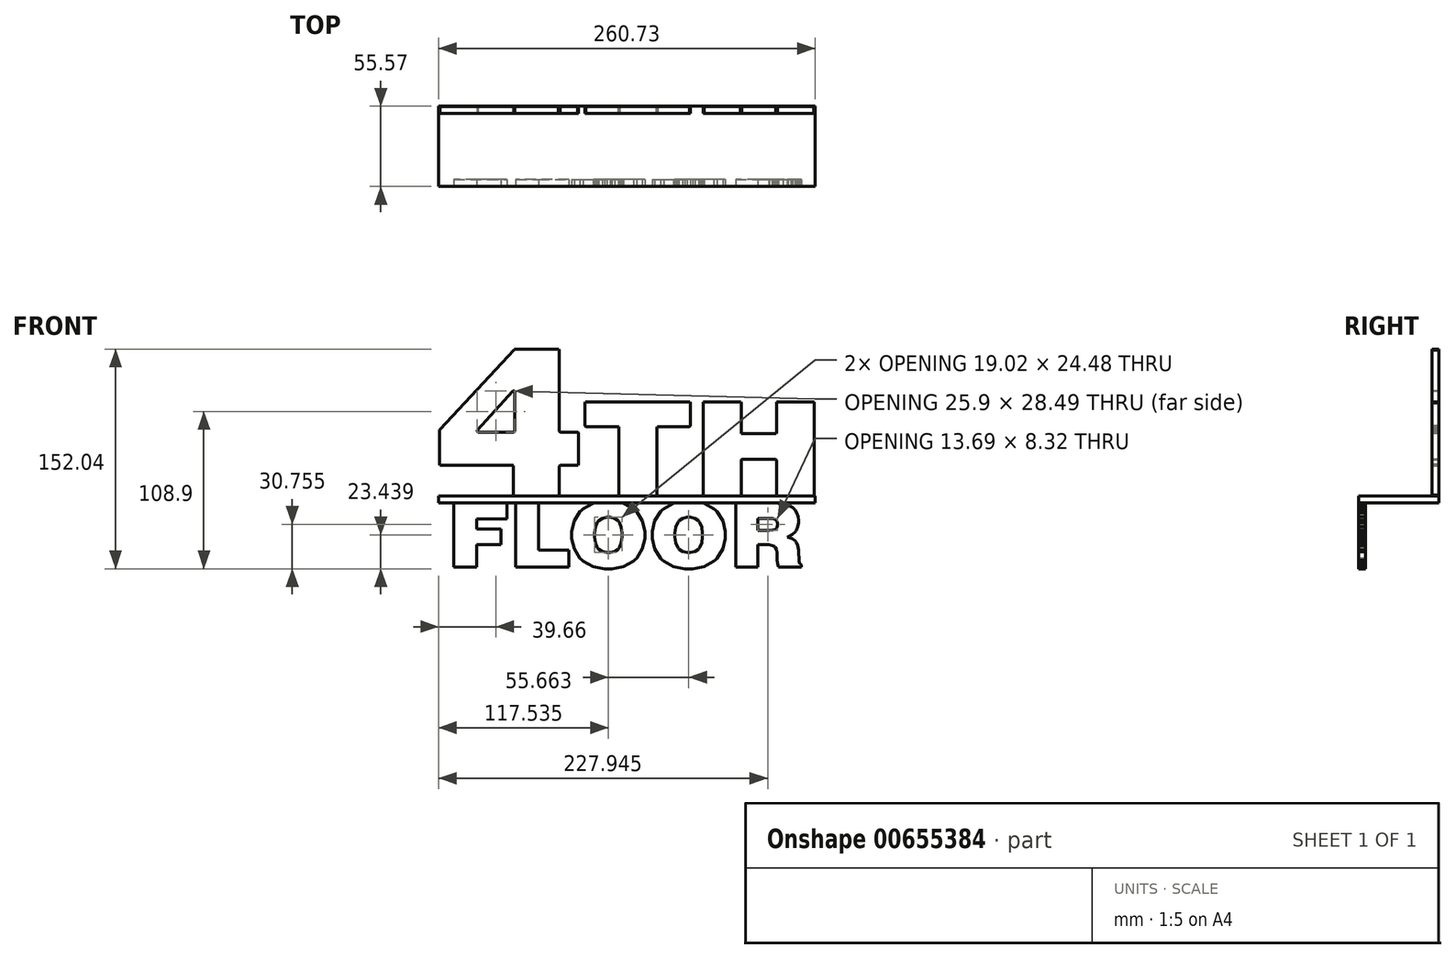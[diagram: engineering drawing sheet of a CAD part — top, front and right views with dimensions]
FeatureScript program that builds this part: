
annotation { "Feature Type Name" : "Feature", "Feature Type Description" : "" }
export const myFeature = defineFeature(function(context is Context, id is Id, definition is map)
    precondition{}
    {
        {
            var Q0;
            Q0=qCreatedBy(makeId("Front.planeOp"),FACE);
            var sketch = newSketch(context, id + "F0", { "sketchPlane" : qUnion([Q0])});
            skLineSegment(sketch, "E0", {"start": v(-106.43, 42.26) * mm, "end": v(-81.93, 42.26) * mm});
            skLineSegment(sketch, "E1", {"start": v(-81.93, 42.26) * mm, "end": v(-81.8, 42.26) * mm});
            skLineSegment(sketch, "E2", {"start": v(-81.8, 42.26) * mm, "end": v(-81.43, 42.48) * mm});
            skLineSegment(sketch, "E3", {"start": v(-81.43, 42.48) * mm, "end": v(-81.22, 42.86) * mm});
            skLineSegment(sketch, "E4", {"start": v(-81.22, 42.86) * mm, "end": v(-81.22, 42.98) * mm});
            skLineSegment(sketch, "E5", {"start": v(-81.22, 42.98) * mm, "end": v(-81.22, 70.06) * mm});
            skLineSegment(sketch, "E6", {"start": v(-81.22, 70.06) * mm, "end": v(-81.22, 70.23) * mm});
            skLineSegment(sketch, "E7", {"start": v(-81.22, 70.23) * mm, "end": v(-81.6, 70.7) * mm});
            skLineSegment(sketch, "E8", {"start": v(-81.6, 70.7) * mm, "end": v(-81.68, 70.73) * mm});
            skLineSegment(sketch, "E9", {"start": v(-81.68, 70.73) * mm, "end": v(-81.75, 70.76) * mm});
            skLineSegment(sketch, "E10", {"start": v(-81.75, 70.76) * mm, "end": v(-82.41, 70.6) * mm});
            skLineSegment(sketch, "E11", {"start": v(-82.41, 70.6) * mm, "end": v(-82.46, 70.54) * mm});
            skLineSegment(sketch, "E12", {"start": v(-82.46, 70.54) * mm, "end": v(-106.97, 43.46) * mm});
            skLineSegment(sketch, "E13", {"start": v(-106.97, 43.46) * mm, "end": v(-107.01, 43.4) * mm});
            skLineSegment(sketch, "E14", {"start": v(-107.01, 43.4) * mm, "end": v(-107.12, 42.75) * mm});
            skLineSegment(sketch, "E15", {"start": v(-107.12, 42.75) * mm, "end": v(-107.1, 42.69) * mm});
            skLineSegment(sketch, "E16", {"start": v(-107.1, 42.69) * mm, "end": v(-107.06, 42.62) * mm});
            skLineSegment(sketch, "E17", {"start": v(-107.06, 42.62) * mm, "end": v(-106.6, 42.26) * mm});
            skLineSegment(sketch, "E18", {"start": v(-106.6, 42.26) * mm, "end": v(-106.43, 42.26) * mm});
            skLineSegment(sketch, "E19", {"start": v(-81.98, -1.24) * mm, "end": v(-81.98, 18.49) * mm});
            skLineSegment(sketch, "E20", {"start": v(-81.98, 18.49) * mm, "end": v(-81.98, 18.61) * mm});
            skLineSegment(sketch, "E21", {"start": v(-81.98, 18.61) * mm, "end": v(-82.2, 19) * mm});
            skLineSegment(sketch, "E22", {"start": v(-82.2, 19) * mm, "end": v(-82.58, 19.2) * mm});
            skLineSegment(sketch, "E23", {"start": v(-82.58, 19.2) * mm, "end": v(-82.7, 19.2) * mm});
            skLineSegment(sketch, "E24", {"start": v(-82.7, 19.2) * mm, "end": v(-132.44, 19.2) * mm});
            skLineSegment(sketch, "E25", {"start": v(-132.44, 19.2) * mm, "end": v(-132.57, 19.2) * mm});
            skLineSegment(sketch, "E26", {"start": v(-132.57, 19.2) * mm, "end": v(-132.95, 19.4) * mm});
            skLineSegment(sketch, "E27", {"start": v(-132.95, 19.4) * mm, "end": v(-133.16, 19.8) * mm});
            skLineSegment(sketch, "E28", {"start": v(-133.16, 19.8) * mm, "end": v(-133.16, 19.92) * mm});
            skLineSegment(sketch, "E29", {"start": v(-133.16, 19.92) * mm, "end": v(-133.16, 43.55) * mm});
            skLineSegment(sketch, "E30", {"start": v(-133.16, 43.55) * mm, "end": v(-133.16, 43.67) * mm});
            skLineSegment(sketch, "E31", {"start": v(-133.16, 43.67) * mm, "end": v(-133, 44) * mm});
            skLineSegment(sketch, "E32", {"start": v(-133, 44) * mm, "end": v(-132.97, 44.04) * mm});
            skLineSegment(sketch, "E33", {"start": v(-132.97, 44.04) * mm, "end": v(-81.43, 99.42) * mm});
            skLineSegment(sketch, "E34", {"start": v(-81.43, 99.42) * mm, "end": v(-81.4, 99.46) * mm});
            skLineSegment(sketch, "E35", {"start": v(-81.4, 99.46) * mm, "end": v(-81.03, 99.65) * mm});
            skLineSegment(sketch, "E36", {"start": v(-81.03, 99.65) * mm, "end": v(-80.9, 99.65) * mm});
            skLineSegment(sketch, "E37", {"start": v(-80.9, 99.65) * mm, "end": v(-51, 99.65) * mm});
            skLineSegment(sketch, "E38", {"start": v(-51, 99.65) * mm, "end": v(-50.88, 99.65) * mm});
            skLineSegment(sketch, "E39", {"start": v(-50.88, 99.65) * mm, "end": v(-50.5, 99.44) * mm});
            skLineSegment(sketch, "E40", {"start": v(-50.5, 99.44) * mm, "end": v(-50.29, 99.06) * mm});
            skLineSegment(sketch, "E41", {"start": v(-50.29, 99.06) * mm, "end": v(-50.29, 98.93) * mm});
            skLineSegment(sketch, "E42", {"start": v(-50.29, 98.93) * mm, "end": v(-50.29, 42.98) * mm});
            skLineSegment(sketch, "E43", {"start": v(-50.29, 42.98) * mm, "end": v(-50.29, 42.86) * mm});
            skLineSegment(sketch, "E44", {"start": v(-50.29, 42.86) * mm, "end": v(-50.08, 42.48) * mm});
            skLineSegment(sketch, "E45", {"start": v(-50.08, 42.48) * mm, "end": v(-49.7, 42.26) * mm});
            skLineSegment(sketch, "E46", {"start": v(-49.7, 42.26) * mm, "end": v(-49.57, 42.26) * mm});
            skLineSegment(sketch, "E47", {"start": v(-49.57, 42.26) * mm, "end": v(-37.82, 42.26) * mm});
            skLineSegment(sketch, "E48", {"start": v(-37.82, 42.26) * mm, "end": v(-37.7, 42.26) * mm});
            skLineSegment(sketch, "E49", {"start": v(-37.7, 42.26) * mm, "end": v(-37.32, 42.05) * mm});
            skLineSegment(sketch, "E50", {"start": v(-37.32, 42.05) * mm, "end": v(-37.1, 41.67) * mm});
            skLineSegment(sketch, "E51", {"start": v(-37.1, 41.67) * mm, "end": v(-37.1, 41.54) * mm});
            skLineSegment(sketch, "E52", {"start": v(-37.1, 41.54) * mm, "end": v(-37.1, 19.92) * mm});
            skLineSegment(sketch, "E53", {"start": v(-37.1, 19.92) * mm, "end": v(-37.1, 19.8) * mm});
            skLineSegment(sketch, "E54", {"start": v(-37.1, 19.8) * mm, "end": v(-37.32, 19.4) * mm});
            skLineSegment(sketch, "E55", {"start": v(-37.32, 19.4) * mm, "end": v(-37.7, 19.2) * mm});
            skLineSegment(sketch, "E56", {"start": v(-37.7, 19.2) * mm, "end": v(-37.82, 19.2) * mm});
            skLineSegment(sketch, "E57", {"start": v(-37.82, 19.2) * mm, "end": v(-49.57, 19.2) * mm});
            skLineSegment(sketch, "E58", {"start": v(-49.57, 19.2) * mm, "end": v(-49.7, 19.2) * mm});
            skLineSegment(sketch, "E59", {"start": v(-49.7, 19.2) * mm, "end": v(-50.08, 19) * mm});
            skLineSegment(sketch, "E60", {"start": v(-50.08, 19) * mm, "end": v(-50.29, 18.61) * mm});
            skLineSegment(sketch, "E61", {"start": v(-50.29, 18.61) * mm, "end": v(-50.29, 18.49) * mm});
            skLineSegment(sketch, "E62", {"start": v(-50.29, 18.49) * mm, "end": v(-50.29, -1.24) * mm});
            skLineSegment(sketch, "E63", {"start": v(-50.29, -1.24) * mm, "end": v(-50.29, -1.36) * mm});
            skLineSegment(sketch, "E64", {"start": v(-50.29, -1.36) * mm, "end": v(-50.5, -1.74) * mm});
            skLineSegment(sketch, "E65", {"start": v(-50.5, -1.74) * mm, "end": v(-50.88, -1.95) * mm});
            skLineSegment(sketch, "E66", {"start": v(-50.88, -1.95) * mm, "end": v(-51, -1.95) * mm});
            skLineSegment(sketch, "E67", {"start": v(-51, -1.95) * mm, "end": v(-81.27, -1.95) * mm});
            skLineSegment(sketch, "E68", {"start": v(-81.27, -1.95) * mm, "end": v(-81.4, -1.95) * mm});
            skLineSegment(sketch, "E69", {"start": v(-81.4, -1.95) * mm, "end": v(-81.77, -1.74) * mm});
            skLineSegment(sketch, "E70", {"start": v(-81.77, -1.74) * mm, "end": v(-81.98, -1.36) * mm});
            skLineSegment(sketch, "E71", {"start": v(-81.98, -1.36) * mm, "end": v(-81.98, -1.24) * mm});
            skLineSegment(sketch, "E72", {"start": v(-8.96, -1.24) * mm, "end": v(-8.96, 45.3) * mm});
            skLineSegment(sketch, "E73", {"start": v(-8.96, 45.3) * mm, "end": v(-8.96, 45.43) * mm});
            skLineSegment(sketch, "E74", {"start": v(-8.96, 45.43) * mm, "end": v(-9.17, 45.81) * mm});
            skLineSegment(sketch, "E75", {"start": v(-9.17, 45.81) * mm, "end": v(-9.55, 46.02) * mm});
            skLineSegment(sketch, "E76", {"start": v(-9.55, 46.02) * mm, "end": v(-9.68, 46.02) * mm});
            skLineSegment(sketch, "E77", {"start": v(-9.68, 46.02) * mm, "end": v(-31.78, 46.02) * mm});
            skLineSegment(sketch, "E78", {"start": v(-31.78, 46.02) * mm, "end": v(-31.91, 46.02) * mm});
            skLineSegment(sketch, "E79", {"start": v(-31.91, 46.02) * mm, "end": v(-32.3, 46.23) * mm});
            skLineSegment(sketch, "E80", {"start": v(-32.3, 46.23) * mm, "end": v(-32.5, 46.61) * mm});
            skLineSegment(sketch, "E81", {"start": v(-32.5, 46.61) * mm, "end": v(-32.5, 46.74) * mm});
            skLineSegment(sketch, "E82", {"start": v(-32.5, 46.74) * mm, "end": v(-32.5, 62.47) * mm});
            skLineSegment(sketch, "E83", {"start": v(-32.5, 62.47) * mm, "end": v(-32.5, 62.6) * mm});
            skLineSegment(sketch, "E84", {"start": v(-32.5, 62.6) * mm, "end": v(-32.3, 62.97) * mm});
            skLineSegment(sketch, "E85", {"start": v(-32.3, 62.97) * mm, "end": v(-31.91, 63.18) * mm});
            skLineSegment(sketch, "E86", {"start": v(-31.91, 63.18) * mm, "end": v(-31.78, 63.18) * mm});
            skLineSegment(sketch, "E87", {"start": v(-31.78, 63.18) * mm, "end": v(39.64, 63.18) * mm});
            skLineSegment(sketch, "E88", {"start": v(39.64, 63.18) * mm, "end": v(39.77, 63.18) * mm});
            skLineSegment(sketch, "E89", {"start": v(39.77, 63.18) * mm, "end": v(40.15, 62.97) * mm});
            skLineSegment(sketch, "E90", {"start": v(40.15, 62.97) * mm, "end": v(40.36, 62.6) * mm});
            skLineSegment(sketch, "E91", {"start": v(40.36, 62.6) * mm, "end": v(40.36, 62.47) * mm});
            skLineSegment(sketch, "E92", {"start": v(40.36, 62.47) * mm, "end": v(40.36, 46.74) * mm});
            skLineSegment(sketch, "E93", {"start": v(40.36, 46.74) * mm, "end": v(40.36, 46.61) * mm});
            skLineSegment(sketch, "E94", {"start": v(40.36, 46.61) * mm, "end": v(40.15, 46.23) * mm});
            skLineSegment(sketch, "E95", {"start": v(40.15, 46.23) * mm, "end": v(39.77, 46.02) * mm});
            skLineSegment(sketch, "E96", {"start": v(39.77, 46.02) * mm, "end": v(39.64, 46.02) * mm});
            skLineSegment(sketch, "E97", {"start": v(39.64, 46.02) * mm, "end": v(18.03, 46.02) * mm});
            skLineSegment(sketch, "E98", {"start": v(18.03, 46.02) * mm, "end": v(17.9, 46.02) * mm});
            skLineSegment(sketch, "E99", {"start": v(17.9, 46.02) * mm, "end": v(17.52, 45.81) * mm});
            skLineSegment(sketch, "E100", {"start": v(17.52, 45.81) * mm, "end": v(17.31, 45.43) * mm});
            skLineSegment(sketch, "E101", {"start": v(17.31, 45.43) * mm, "end": v(17.31, 45.3) * mm});
            skLineSegment(sketch, "E102", {"start": v(17.31, 45.3) * mm, "end": v(17.31, -1.24) * mm});
            skLineSegment(sketch, "E103", {"start": v(17.31, -1.24) * mm, "end": v(17.31, -1.36) * mm});
            skLineSegment(sketch, "E104", {"start": v(17.31, -1.36) * mm, "end": v(17.1, -1.75) * mm});
            skLineSegment(sketch, "E105", {"start": v(17.1, -1.75) * mm, "end": v(16.72, -1.96) * mm});
            skLineSegment(sketch, "E106", {"start": v(16.72, -1.96) * mm, "end": v(16.6, -1.96) * mm});
            skLineSegment(sketch, "E107", {"start": v(16.6, -1.96) * mm, "end": v(-8.24, -1.96) * mm});
            skLineSegment(sketch, "E108", {"start": v(-8.24, -1.96) * mm, "end": v(-8.37, -1.96) * mm});
            skLineSegment(sketch, "E109", {"start": v(-8.37, -1.96) * mm, "end": v(-8.75, -1.75) * mm});
            skLineSegment(sketch, "E110", {"start": v(-8.75, -1.75) * mm, "end": v(-8.96, -1.36) * mm});
            skLineSegment(sketch, "E111", {"start": v(-8.96, -1.36) * mm, "end": v(-8.96, -1.24) * mm});
            skLineSegment(sketch, "E112", {"start": v(49.34, -1.24) * mm, "end": v(49.34, 62.47) * mm});
            skLineSegment(sketch, "E113", {"start": v(49.34, 62.47) * mm, "end": v(49.34, 62.6) * mm});
            skLineSegment(sketch, "E114", {"start": v(49.34, 62.6) * mm, "end": v(49.55, 62.97) * mm});
            skLineSegment(sketch, "E115", {"start": v(49.55, 62.97) * mm, "end": v(49.93, 63.18) * mm});
            skLineSegment(sketch, "E116", {"start": v(49.93, 63.18) * mm, "end": v(50.06, 63.18) * mm});
            skLineSegment(sketch, "E117", {"start": v(50.06, 63.18) * mm, "end": v(74.9, 63.18) * mm});
            skLineSegment(sketch, "E118", {"start": v(74.9, 63.18) * mm, "end": v(75.02, 63.18) * mm});
            skLineSegment(sketch, "E119", {"start": v(75.02, 63.18) * mm, "end": v(75.4, 62.97) * mm});
            skLineSegment(sketch, "E120", {"start": v(75.4, 62.97) * mm, "end": v(75.61, 62.6) * mm});
            skLineSegment(sketch, "E121", {"start": v(75.61, 62.6) * mm, "end": v(75.61, 62.47) * mm});
            skLineSegment(sketch, "E122", {"start": v(75.61, 62.47) * mm, "end": v(75.61, 41.78) * mm});
            skLineSegment(sketch, "E123", {"start": v(75.61, 41.78) * mm, "end": v(75.61, 41.66) * mm});
            skLineSegment(sketch, "E124", {"start": v(75.61, 41.66) * mm, "end": v(75.82, 41.28) * mm});
            skLineSegment(sketch, "E125", {"start": v(75.82, 41.28) * mm, "end": v(76.2, 41.07) * mm});
            skLineSegment(sketch, "E126", {"start": v(76.2, 41.07) * mm, "end": v(76.33, 41.07) * mm});
            skLineSegment(sketch, "E127", {"start": v(76.33, 41.07) * mm, "end": v(99.37, 41.07) * mm});
            skLineSegment(sketch, "E128", {"start": v(99.37, 41.07) * mm, "end": v(99.5, 41.07) * mm});
            skLineSegment(sketch, "E129", {"start": v(99.5, 41.07) * mm, "end": v(99.88, 41.28) * mm});
            skLineSegment(sketch, "E130", {"start": v(99.88, 41.28) * mm, "end": v(100.09, 41.66) * mm});
            skLineSegment(sketch, "E131", {"start": v(100.09, 41.66) * mm, "end": v(100.09, 41.78) * mm});
            skLineSegment(sketch, "E132", {"start": v(100.09, 41.78) * mm, "end": v(100.09, 62.47) * mm});
            skLineSegment(sketch, "E133", {"start": v(100.09, 62.47) * mm, "end": v(100.09, 62.6) * mm});
            skLineSegment(sketch, "E134", {"start": v(100.09, 62.6) * mm, "end": v(100.3, 62.97) * mm});
            skLineSegment(sketch, "E135", {"start": v(100.3, 62.97) * mm, "end": v(100.67, 63.18) * mm});
            skLineSegment(sketch, "E136", {"start": v(100.67, 63.18) * mm, "end": v(100.8, 63.18) * mm});
            skLineSegment(sketch, "E137", {"start": v(100.8, 63.18) * mm, "end": v(125.64, 63.18) * mm});
            skLineSegment(sketch, "E138", {"start": v(125.64, 63.18) * mm, "end": v(125.77, 63.18) * mm});
            skLineSegment(sketch, "E139", {"start": v(125.77, 63.18) * mm, "end": v(126.15, 62.97) * mm});
            skLineSegment(sketch, "E140", {"start": v(126.15, 62.97) * mm, "end": v(126.36, 62.6) * mm});
            skLineSegment(sketch, "E141", {"start": v(126.36, 62.6) * mm, "end": v(126.36, 62.47) * mm});
            skLineSegment(sketch, "E142", {"start": v(126.36, 62.47) * mm, "end": v(126.36, -1.24) * mm});
            skLineSegment(sketch, "E143", {"start": v(126.36, -1.24) * mm, "end": v(126.36, -1.36) * mm});
            skLineSegment(sketch, "E144", {"start": v(126.36, -1.36) * mm, "end": v(126.15, -1.75) * mm});
            skLineSegment(sketch, "E145", {"start": v(126.15, -1.75) * mm, "end": v(125.77, -1.96) * mm});
            skLineSegment(sketch, "E146", {"start": v(125.77, -1.96) * mm, "end": v(125.64, -1.96) * mm});
            skLineSegment(sketch, "E147", {"start": v(125.64, -1.96) * mm, "end": v(100.8, -1.96) * mm});
            skLineSegment(sketch, "E148", {"start": v(100.8, -1.96) * mm, "end": v(100.67, -1.96) * mm});
            skLineSegment(sketch, "E149", {"start": v(100.67, -1.96) * mm, "end": v(100.3, -1.75) * mm});
            skLineSegment(sketch, "E150", {"start": v(100.3, -1.75) * mm, "end": v(100.09, -1.36) * mm});
            skLineSegment(sketch, "E151", {"start": v(100.09, -1.36) * mm, "end": v(100.09, -1.24) * mm});
            skLineSegment(sketch, "E152", {"start": v(100.09, -1.24) * mm, "end": v(100.09, 22.57) * mm});
            skLineSegment(sketch, "E153", {"start": v(100.09, 22.57) * mm, "end": v(100.09, 22.7) * mm});
            skLineSegment(sketch, "E154", {"start": v(100.09, 22.7) * mm, "end": v(99.88, 23.07) * mm});
            skLineSegment(sketch, "E155", {"start": v(99.88, 23.07) * mm, "end": v(99.5, 23.28) * mm});
            skLineSegment(sketch, "E156", {"start": v(99.5, 23.28) * mm, "end": v(99.37, 23.28) * mm});
            skLineSegment(sketch, "E157", {"start": v(99.37, 23.28) * mm, "end": v(76.33, 23.28) * mm});
            skLineSegment(sketch, "E158", {"start": v(76.33, 23.28) * mm, "end": v(76.2, 23.28) * mm});
            skLineSegment(sketch, "E159", {"start": v(76.2, 23.28) * mm, "end": v(75.82, 23.07) * mm});
            skLineSegment(sketch, "E160", {"start": v(75.82, 23.07) * mm, "end": v(75.61, 22.7) * mm});
            skLineSegment(sketch, "E161", {"start": v(75.61, 22.7) * mm, "end": v(75.61, 22.57) * mm});
            skLineSegment(sketch, "E162", {"start": v(75.61, 22.57) * mm, "end": v(75.61, -1.24) * mm});
            skLineSegment(sketch, "E163", {"start": v(75.61, -1.24) * mm, "end": v(75.61, -1.36) * mm});
            skLineSegment(sketch, "E164", {"start": v(75.61, -1.36) * mm, "end": v(75.4, -1.75) * mm});
            skLineSegment(sketch, "E165", {"start": v(75.4, -1.75) * mm, "end": v(75.02, -1.96) * mm});
            skLineSegment(sketch, "E166", {"start": v(75.02, -1.96) * mm, "end": v(74.9, -1.96) * mm});
            skLineSegment(sketch, "E167", {"start": v(74.9, -1.96) * mm, "end": v(50.06, -1.96) * mm});
            skLineSegment(sketch, "E168", {"start": v(50.06, -1.96) * mm, "end": v(49.93, -1.96) * mm});
            skLineSegment(sketch, "E169", {"start": v(49.93, -1.96) * mm, "end": v(49.55, -1.75) * mm});
            skLineSegment(sketch, "E170", {"start": v(49.55, -1.75) * mm, "end": v(49.34, -1.36) * mm});
            skLineSegment(sketch, "E171", {"start": v(49.34, -1.36) * mm, "end": v(49.34, -1.24) * mm});
            skLineSegment(sketch, "E172", {"start": v(-27.6, -75.9) * mm, "end": v(-27.6, -44.7) * mm});
            skLineSegment(sketch, "E173", {"start": v(-27.6, -44.7) * mm, "end": v(-1.73, -44.7) * mm});
            skLineSegment(sketch, "E174", {"start": v(-1.73, -44.7) * mm, "end": v(-1.73, -52.55) * mm});
            skLineSegment(sketch, "E175", {"start": v(-1.73, -52.55) * mm, "end": v(-16.61, -52.55) * mm});
            skLineSegment(sketch, "E176", {"start": v(-16.61, -52.55) * mm, "end": v(-16.61, -57.38) * mm});
            skLineSegment(sketch, "E177", {"start": v(-16.61, -57.38) * mm, "end": v(-4.78, -57.38) * mm});
            skLineSegment(sketch, "E178", {"start": v(-4.78, -57.38) * mm, "end": v(-4.78, -64.93) * mm});
            skLineSegment(sketch, "E179", {"start": v(-4.78, -64.93) * mm, "end": v(-16.61, -64.93) * mm});
            skLineSegment(sketch, "E180", {"start": v(-16.61, -64.93) * mm, "end": v(-16.61, -75.9) * mm});
            skLineSegment(sketch, "E181", {"start": v(-16.61, -75.9) * mm, "end": v(-27.6, -75.9) * mm});
            skLineSegment(sketch, "E182", {"start": v(2.45, -75.9) * mm, "end": v(2.45, -44.7) * mm});
            skLineSegment(sketch, "E183", {"start": v(2.45, -44.7) * mm, "end": v(13.43, -44.7) * mm});
            skLineSegment(sketch, "E184", {"start": v(13.43, -44.7) * mm, "end": v(13.43, -67.61) * mm});
            skLineSegment(sketch, "E185", {"start": v(13.43, -67.61) * mm, "end": v(28.36, -67.61) * mm});
            skLineSegment(sketch, "E186", {"start": v(28.36, -67.61) * mm, "end": v(28.36, -75.9) * mm});
            skLineSegment(sketch, "E187", {"start": v(28.36, -75.9) * mm, "end": v(2.45, -75.9) * mm});
            skLineSegment(sketch, "E188", {"start": v(40.75, -60.32) * mm, "end": v(40.75, -61.28) * mm});
            skLineSegment(sketch, "E189", {"start": v(40.75, -61.28) * mm, "end": v(41.15, -64.16) * mm});
            skLineSegment(sketch, "E190", {"start": v(41.15, -64.16) * mm, "end": v(42.1, -66.48) * mm});
            skLineSegment(sketch, "E191", {"start": v(42.1, -66.48) * mm, "end": v(42.38, -66.83) * mm});
            skLineSegment(sketch, "E192", {"start": v(42.38, -66.83) * mm, "end": v(42.65, -67.18) * mm});
            skLineSegment(sketch, "E193", {"start": v(42.65, -67.18) * mm, "end": v(44.46, -68.38) * mm});
            skLineSegment(sketch, "E194", {"start": v(44.46, -68.38) * mm, "end": v(46.71, -68.9) * mm});
            skLineSegment(sketch, "E195", {"start": v(46.71, -68.9) * mm, "end": v(47.46, -68.9) * mm});
            skLineSegment(sketch, "E196", {"start": v(47.46, -68.9) * mm, "end": v(48.2, -68.9) * mm});
            skLineSegment(sketch, "E197", {"start": v(48.2, -68.9) * mm, "end": v(50.44, -68.39) * mm});
            skLineSegment(sketch, "E198", {"start": v(50.44, -68.39) * mm, "end": v(52.23, -67.18) * mm});
            skLineSegment(sketch, "E199", {"start": v(52.23, -67.18) * mm, "end": v(52.5, -66.84) * mm});
            skLineSegment(sketch, "E200", {"start": v(52.5, -66.84) * mm, "end": v(52.77, -66.5) * mm});
            skLineSegment(sketch, "E201", {"start": v(52.77, -66.5) * mm, "end": v(53.7, -64.18) * mm});
            skLineSegment(sketch, "E202", {"start": v(53.7, -64.18) * mm, "end": v(54.1, -61.28) * mm});
            skLineSegment(sketch, "E203", {"start": v(54.1, -61.28) * mm, "end": v(54.1, -60.32) * mm});
            skLineSegment(sketch, "E204", {"start": v(54.1, -60.32) * mm, "end": v(54.1, -59.35) * mm});
            skLineSegment(sketch, "E205", {"start": v(54.1, -59.35) * mm, "end": v(53.7, -56.45) * mm});
            skLineSegment(sketch, "E206", {"start": v(53.7, -56.45) * mm, "end": v(52.77, -54.13) * mm});
            skLineSegment(sketch, "E207", {"start": v(52.77, -54.13) * mm, "end": v(52.5, -53.79) * mm});
            skLineSegment(sketch, "E208", {"start": v(52.5, -53.79) * mm, "end": v(52.23, -53.44) * mm});
            skLineSegment(sketch, "E209", {"start": v(52.23, -53.44) * mm, "end": v(50.44, -52.23) * mm});
            skLineSegment(sketch, "E210", {"start": v(50.44, -52.23) * mm, "end": v(48.2, -51.72) * mm});
            skLineSegment(sketch, "E211", {"start": v(48.2, -51.72) * mm, "end": v(47.46, -51.72) * mm});
            skLineSegment(sketch, "E212", {"start": v(47.46, -51.72) * mm, "end": v(46.71, -51.72) * mm});
            skLineSegment(sketch, "E213", {"start": v(46.71, -51.72) * mm, "end": v(44.46, -52.24) * mm});
            skLineSegment(sketch, "E214", {"start": v(44.46, -52.24) * mm, "end": v(42.65, -53.45) * mm});
            skLineSegment(sketch, "E215", {"start": v(42.65, -53.45) * mm, "end": v(42.38, -53.8) * mm});
            skLineSegment(sketch, "E216", {"start": v(42.38, -53.8) * mm, "end": v(42.1, -54.14) * mm});
            skLineSegment(sketch, "E217", {"start": v(42.1, -54.14) * mm, "end": v(41.15, -56.47) * mm});
            skLineSegment(sketch, "E218", {"start": v(41.15, -56.47) * mm, "end": v(40.75, -59.35) * mm});
            skLineSegment(sketch, "E219", {"start": v(40.75, -59.35) * mm, "end": v(40.75, -60.32) * mm});
            skLineSegment(sketch, "E220", {"start": v(29.68, -60.32) * mm, "end": v(29.68, -58.61) * mm});
            skLineSegment(sketch, "E221", {"start": v(29.68, -58.61) * mm, "end": v(30.87, -53.5) * mm});
            skLineSegment(sketch, "E222", {"start": v(30.87, -53.5) * mm, "end": v(33.66, -49.02) * mm});
            skLineSegment(sketch, "E223", {"start": v(33.66, -49.02) * mm, "end": v(34.45, -48.29) * mm});
            skLineSegment(sketch, "E224", {"start": v(34.45, -48.29) * mm, "end": v(35.24, -47.55) * mm});
            skLineSegment(sketch, "E225", {"start": v(35.24, -47.55) * mm, "end": v(40.1, -44.98) * mm});
            skLineSegment(sketch, "E226", {"start": v(40.1, -44.98) * mm, "end": v(45.62, -43.88) * mm});
            skLineSegment(sketch, "E227", {"start": v(45.62, -43.88) * mm, "end": v(47.46, -43.88) * mm});
            skLineSegment(sketch, "E228", {"start": v(47.46, -43.88) * mm, "end": v(49.3, -43.88) * mm});
            skLineSegment(sketch, "E229", {"start": v(49.3, -43.88) * mm, "end": v(54.81, -44.98) * mm});
            skLineSegment(sketch, "E230", {"start": v(54.81, -44.98) * mm, "end": v(59.64, -47.55) * mm});
            skLineSegment(sketch, "E231", {"start": v(59.64, -47.55) * mm, "end": v(60.44, -48.29) * mm});
            skLineSegment(sketch, "E232", {"start": v(60.44, -48.29) * mm, "end": v(61.23, -49.02) * mm});
            skLineSegment(sketch, "E233", {"start": v(61.23, -49.02) * mm, "end": v(64, -53.5) * mm});
            skLineSegment(sketch, "E234", {"start": v(64, -53.5) * mm, "end": v(65.2, -58.61) * mm});
            skLineSegment(sketch, "E235", {"start": v(65.2, -58.61) * mm, "end": v(65.2, -60.32) * mm});
            skLineSegment(sketch, "E236", {"start": v(65.2, -60.32) * mm, "end": v(65.2, -62.02) * mm});
            skLineSegment(sketch, "E237", {"start": v(65.2, -62.02) * mm, "end": v(64, -67.13) * mm});
            skLineSegment(sketch, "E238", {"start": v(64, -67.13) * mm, "end": v(61.23, -71.61) * mm});
            skLineSegment(sketch, "E239", {"start": v(61.23, -71.61) * mm, "end": v(60.44, -72.35) * mm});
            skLineSegment(sketch, "E240", {"start": v(60.44, -72.35) * mm, "end": v(59.64, -73.08) * mm});
            skLineSegment(sketch, "E241", {"start": v(59.64, -73.08) * mm, "end": v(54.81, -75.66) * mm});
            skLineSegment(sketch, "E242", {"start": v(54.81, -75.66) * mm, "end": v(49.3, -76.77) * mm});
            skLineSegment(sketch, "E243", {"start": v(49.3, -76.77) * mm, "end": v(47.46, -76.77) * mm});
            skLineSegment(sketch, "E244", {"start": v(47.46, -76.77) * mm, "end": v(45.62, -76.77) * mm});
            skLineSegment(sketch, "E245", {"start": v(45.62, -76.77) * mm, "end": v(40.1, -75.66) * mm});
            skLineSegment(sketch, "E246", {"start": v(40.1, -75.66) * mm, "end": v(35.24, -73.08) * mm});
            skLineSegment(sketch, "E247", {"start": v(35.24, -73.08) * mm, "end": v(34.45, -72.35) * mm});
            skLineSegment(sketch, "E248", {"start": v(34.45, -72.35) * mm, "end": v(33.66, -71.61) * mm});
            skLineSegment(sketch, "E249", {"start": v(33.66, -71.61) * mm, "end": v(30.87, -67.13) * mm});
            skLineSegment(sketch, "E250", {"start": v(30.87, -67.13) * mm, "end": v(29.68, -62.02) * mm});
            skLineSegment(sketch, "E251", {"start": v(29.68, -62.02) * mm, "end": v(29.68, -60.32) * mm});
            skLineSegment(sketch, "E252", {"start": v(79.83, -60.32) * mm, "end": v(79.83, -61.28) * mm});
            skLineSegment(sketch, "E253", {"start": v(79.83, -61.28) * mm, "end": v(80.23, -64.16) * mm});
            skLineSegment(sketch, "E254", {"start": v(80.23, -64.16) * mm, "end": v(81.18, -66.48) * mm});
            skLineSegment(sketch, "E255", {"start": v(81.18, -66.48) * mm, "end": v(81.45, -66.83) * mm});
            skLineSegment(sketch, "E256", {"start": v(81.45, -66.83) * mm, "end": v(81.72, -67.18) * mm});
            skLineSegment(sketch, "E257", {"start": v(81.72, -67.18) * mm, "end": v(83.54, -68.38) * mm});
            skLineSegment(sketch, "E258", {"start": v(83.54, -68.38) * mm, "end": v(85.79, -68.9) * mm});
            skLineSegment(sketch, "E259", {"start": v(85.79, -68.9) * mm, "end": v(86.54, -68.9) * mm});
            skLineSegment(sketch, "E260", {"start": v(86.54, -68.9) * mm, "end": v(87.28, -68.9) * mm});
            skLineSegment(sketch, "E261", {"start": v(87.28, -68.9) * mm, "end": v(89.52, -68.39) * mm});
            skLineSegment(sketch, "E262", {"start": v(89.52, -68.39) * mm, "end": v(91.31, -67.18) * mm});
            skLineSegment(sketch, "E263", {"start": v(91.31, -67.18) * mm, "end": v(91.58, -66.84) * mm});
            skLineSegment(sketch, "E264", {"start": v(91.58, -66.84) * mm, "end": v(91.85, -66.5) * mm});
            skLineSegment(sketch, "E265", {"start": v(91.85, -66.5) * mm, "end": v(92.78, -64.18) * mm});
            skLineSegment(sketch, "E266", {"start": v(92.78, -64.18) * mm, "end": v(93.18, -61.28) * mm});
            skLineSegment(sketch, "E267", {"start": v(93.18, -61.28) * mm, "end": v(93.18, -60.32) * mm});
            skLineSegment(sketch, "E268", {"start": v(93.18, -60.32) * mm, "end": v(93.18, -59.35) * mm});
            skLineSegment(sketch, "E269", {"start": v(93.18, -59.35) * mm, "end": v(92.78, -56.45) * mm});
            skLineSegment(sketch, "E270", {"start": v(92.78, -56.45) * mm, "end": v(91.85, -54.13) * mm});
            skLineSegment(sketch, "E271", {"start": v(91.85, -54.13) * mm, "end": v(91.58, -53.79) * mm});
            skLineSegment(sketch, "E272", {"start": v(91.58, -53.79) * mm, "end": v(91.31, -53.44) * mm});
            skLineSegment(sketch, "E273", {"start": v(91.31, -53.44) * mm, "end": v(89.52, -52.23) * mm});
            skLineSegment(sketch, "E274", {"start": v(89.52, -52.23) * mm, "end": v(87.28, -51.72) * mm});
            skLineSegment(sketch, "E275", {"start": v(87.28, -51.72) * mm, "end": v(86.54, -51.72) * mm});
            skLineSegment(sketch, "E276", {"start": v(86.54, -51.72) * mm, "end": v(85.79, -51.72) * mm});
            skLineSegment(sketch, "E277", {"start": v(85.79, -51.72) * mm, "end": v(83.54, -52.24) * mm});
            skLineSegment(sketch, "E278", {"start": v(83.54, -52.24) * mm, "end": v(81.72, -53.45) * mm});
            skLineSegment(sketch, "E279", {"start": v(81.72, -53.45) * mm, "end": v(81.45, -53.8) * mm});
            skLineSegment(sketch, "E280", {"start": v(81.45, -53.8) * mm, "end": v(81.18, -54.14) * mm});
            skLineSegment(sketch, "E281", {"start": v(81.18, -54.14) * mm, "end": v(80.23, -56.47) * mm});
            skLineSegment(sketch, "E282", {"start": v(80.23, -56.47) * mm, "end": v(79.83, -59.35) * mm});
            skLineSegment(sketch, "E283", {"start": v(79.83, -59.35) * mm, "end": v(79.83, -60.32) * mm});
            skLineSegment(sketch, "E284", {"start": v(68.76, -60.32) * mm, "end": v(68.76, -58.61) * mm});
            skLineSegment(sketch, "E285", {"start": v(68.76, -58.61) * mm, "end": v(69.95, -53.5) * mm});
            skLineSegment(sketch, "E286", {"start": v(69.95, -53.5) * mm, "end": v(72.73, -49.02) * mm});
            skLineSegment(sketch, "E287", {"start": v(72.73, -49.02) * mm, "end": v(73.53, -48.29) * mm});
            skLineSegment(sketch, "E288", {"start": v(73.53, -48.29) * mm, "end": v(74.32, -47.55) * mm});
            skLineSegment(sketch, "E289", {"start": v(74.32, -47.55) * mm, "end": v(79.16, -44.98) * mm});
            skLineSegment(sketch, "E290", {"start": v(79.16, -44.98) * mm, "end": v(84.7, -43.88) * mm});
            skLineSegment(sketch, "E291", {"start": v(84.7, -43.88) * mm, "end": v(86.54, -43.88) * mm});
            skLineSegment(sketch, "E292", {"start": v(86.54, -43.88) * mm, "end": v(88.37, -43.88) * mm});
            skLineSegment(sketch, "E293", {"start": v(88.37, -43.88) * mm, "end": v(93.9, -44.98) * mm});
            skLineSegment(sketch, "E294", {"start": v(93.9, -44.98) * mm, "end": v(98.72, -47.55) * mm});
            skLineSegment(sketch, "E295", {"start": v(98.72, -47.55) * mm, "end": v(99.51, -48.29) * mm});
            skLineSegment(sketch, "E296", {"start": v(99.51, -48.29) * mm, "end": v(100.3, -49.02) * mm});
            skLineSegment(sketch, "E297", {"start": v(100.3, -49.02) * mm, "end": v(103.08, -53.5) * mm});
            skLineSegment(sketch, "E298", {"start": v(103.08, -53.5) * mm, "end": v(104.27, -58.61) * mm});
            skLineSegment(sketch, "E299", {"start": v(104.27, -58.61) * mm, "end": v(104.27, -60.32) * mm});
            skLineSegment(sketch, "E300", {"start": v(104.27, -60.32) * mm, "end": v(104.27, -62.02) * mm});
            skLineSegment(sketch, "E301", {"start": v(104.27, -62.02) * mm, "end": v(103.08, -67.13) * mm});
            skLineSegment(sketch, "E302", {"start": v(103.08, -67.13) * mm, "end": v(100.3, -71.61) * mm});
            skLineSegment(sketch, "E303", {"start": v(100.3, -71.61) * mm, "end": v(99.51, -72.35) * mm});
            skLineSegment(sketch, "E304", {"start": v(99.51, -72.35) * mm, "end": v(98.72, -73.08) * mm});
            skLineSegment(sketch, "E305", {"start": v(98.72, -73.08) * mm, "end": v(93.9, -75.66) * mm});
            skLineSegment(sketch, "E306", {"start": v(93.9, -75.66) * mm, "end": v(88.37, -76.77) * mm});
            skLineSegment(sketch, "E307", {"start": v(88.37, -76.77) * mm, "end": v(86.54, -76.77) * mm});
            skLineSegment(sketch, "E308", {"start": v(86.54, -76.77) * mm, "end": v(84.7, -76.77) * mm});
            skLineSegment(sketch, "E309", {"start": v(84.7, -76.77) * mm, "end": v(79.16, -75.66) * mm});
            skLineSegment(sketch, "E310", {"start": v(79.16, -75.66) * mm, "end": v(74.32, -73.08) * mm});
            skLineSegment(sketch, "E311", {"start": v(74.32, -73.08) * mm, "end": v(73.53, -72.35) * mm});
            skLineSegment(sketch, "E312", {"start": v(73.53, -72.35) * mm, "end": v(72.73, -71.61) * mm});
            skLineSegment(sketch, "E313", {"start": v(72.73, -71.61) * mm, "end": v(69.95, -67.13) * mm});
            skLineSegment(sketch, "E314", {"start": v(69.95, -67.13) * mm, "end": v(68.76, -62.02) * mm});
            skLineSegment(sketch, "E315", {"start": v(68.76, -62.02) * mm, "end": v(68.76, -60.32) * mm});
            skLineSegment(sketch, "E316", {"start": v(120.13, -58.1) * mm, "end": v(125.12, -58.1) * mm});
            skLineSegment(sketch, "E317", {"start": v(125.12, -58.1) * mm, "end": v(125.68, -58.1) * mm});
            skLineSegment(sketch, "E318", {"start": v(125.68, -58.1) * mm, "end": v(127.34, -57.94) * mm});
            skLineSegment(sketch, "E319", {"start": v(127.34, -57.94) * mm, "end": v(128.58, -57.56) * mm});
            skLineSegment(sketch, "E320", {"start": v(128.58, -57.56) * mm, "end": v(128.75, -57.46) * mm});
            skLineSegment(sketch, "E321", {"start": v(128.75, -57.46) * mm, "end": v(128.91, -57.35) * mm});
            skLineSegment(sketch, "E322", {"start": v(128.91, -57.35) * mm, "end": v(129.5, -56.57) * mm});
            skLineSegment(sketch, "E323", {"start": v(129.5, -56.57) * mm, "end": v(129.75, -55.54) * mm});
            skLineSegment(sketch, "E324", {"start": v(129.75, -55.54) * mm, "end": v(129.75, -55.2) * mm});
            skLineSegment(sketch, "E325", {"start": v(129.75, -55.2) * mm, "end": v(129.75, -54.85) * mm});
            skLineSegment(sketch, "E326", {"start": v(129.75, -54.85) * mm, "end": v(129.5, -53.8) * mm});
            skLineSegment(sketch, "E327", {"start": v(129.5, -53.8) * mm, "end": v(128.91, -53) * mm});
            skLineSegment(sketch, "E328", {"start": v(128.91, -53) * mm, "end": v(128.75, -52.9) * mm});
            skLineSegment(sketch, "E329", {"start": v(128.75, -52.9) * mm, "end": v(128.58, -52.8) * mm});
            skLineSegment(sketch, "E330", {"start": v(128.58, -52.8) * mm, "end": v(127.27, -52.42) * mm});
            skLineSegment(sketch, "E331", {"start": v(127.27, -52.42) * mm, "end": v(125.45, -52.25) * mm});
            skLineSegment(sketch, "E332", {"start": v(125.45, -52.25) * mm, "end": v(124.85, -52.25) * mm});
            skLineSegment(sketch, "E333", {"start": v(124.85, -52.25) * mm, "end": v(120.13, -52.25) * mm});
            skLineSegment(sketch, "E334", {"start": v(120.13, -52.25) * mm, "end": v(120.13, -58.1) * mm});
            skLineSegment(sketch, "E335", {"start": v(109.3, -75.9) * mm, "end": v(109.3, -44.69) * mm});
            skLineSegment(sketch, "E336", {"start": v(109.3, -44.69) * mm, "end": v(125.66, -44.69) * mm});
            skLineSegment(sketch, "E337", {"start": v(125.66, -44.69) * mm, "end": v(127.3, -44.69) * mm});
            skLineSegment(sketch, "E338", {"start": v(127.3, -44.69) * mm, "end": v(132.24, -45.22) * mm});
            skLineSegment(sketch, "E339", {"start": v(132.24, -45.22) * mm, "end": v(136.08, -46.44) * mm});
            skLineSegment(sketch, "E340", {"start": v(136.08, -46.44) * mm, "end": v(136.63, -46.79) * mm});
            skLineSegment(sketch, "E341", {"start": v(136.63, -46.79) * mm, "end": v(137.02, -47.04) * mm});
            skLineSegment(sketch, "E342", {"start": v(137.02, -47.04) * mm, "end": v(138.06, -48) * mm});
            skLineSegment(sketch, "E343", {"start": v(138.06, -48) * mm, "end": v(139.1, -49.56) * mm});
            skLineSegment(sketch, "E344", {"start": v(139.1, -49.56) * mm, "end": v(139.7, -51.45) * mm});
            skLineSegment(sketch, "E345", {"start": v(139.7, -51.45) * mm, "end": v(139.91, -53.12) * mm});
            skLineSegment(sketch, "E346", {"start": v(139.91, -53.12) * mm, "end": v(139.91, -53.67) * mm});
            skLineSegment(sketch, "E347", {"start": v(139.91, -53.67) * mm, "end": v(139.91, -54.33) * mm});
            skLineSegment(sketch, "E348", {"start": v(139.91, -54.33) * mm, "end": v(139.57, -56.29) * mm});
            skLineSegment(sketch, "E349", {"start": v(139.57, -56.29) * mm, "end": v(138.79, -58.1) * mm});
            skLineSegment(sketch, "E350", {"start": v(138.79, -58.1) * mm, "end": v(138.56, -58.42) * mm});
            skLineSegment(sketch, "E351", {"start": v(138.56, -58.42) * mm, "end": v(138.34, -58.73) * mm});
            skLineSegment(sketch, "E352", {"start": v(138.34, -58.73) * mm, "end": v(136.85, -60.1) * mm});
            skLineSegment(sketch, "E353", {"start": v(136.85, -60.1) * mm, "end": v(134.88, -61.22) * mm});
            skLineSegment(sketch, "E354", {"start": v(134.88, -61.22) * mm, "end": v(134.41, -61.4) * mm});
            skLineSegment(sketch, "E355", {"start": v(134.41, -61.4) * mm, "end": v(134.89, -61.5) * mm});
            skLineSegment(sketch, "E356", {"start": v(134.89, -61.5) * mm, "end": v(136.88, -62.23) * mm});
            skLineSegment(sketch, "E357", {"start": v(136.88, -62.23) * mm, "end": v(138.34, -63.3) * mm});
            skLineSegment(sketch, "E358", {"start": v(138.34, -63.3) * mm, "end": v(138.56, -63.58) * mm});
            skLineSegment(sketch, "E359", {"start": v(138.56, -63.58) * mm, "end": v(138.78, -63.85) * mm});
            skLineSegment(sketch, "E360", {"start": v(138.78, -63.85) * mm, "end": v(139.56, -65.58) * mm});
            skLineSegment(sketch, "E361", {"start": v(139.56, -65.58) * mm, "end": v(139.94, -67.81) * mm});
            skLineSegment(sketch, "E362", {"start": v(139.94, -67.81) * mm, "end": v(139.96, -68.34) * mm});
            skLineSegment(sketch, "E363", {"start": v(139.96, -68.34) * mm, "end": v(140.14, -72.68) * mm});
            skLineSegment(sketch, "E364", {"start": v(140.14, -72.68) * mm, "end": v(140.14, -72.7) * mm});
            skLineSegment(sketch, "E365", {"start": v(140.14, -72.7) * mm, "end": v(140.16, -72.77) * mm});
            skLineSegment(sketch, "E366", {"start": v(140.16, -72.77) * mm, "end": v(140.17, -72.78) * mm});
            skLineSegment(sketch, "E367", {"start": v(140.17, -72.78) * mm, "end": v(140.18, -73.1) * mm});
            skLineSegment(sketch, "E368", {"start": v(140.18, -73.1) * mm, "end": v(140.44, -74.2) * mm});
            skLineSegment(sketch, "E369", {"start": v(140.44, -74.2) * mm, "end": v(140.99, -74.72) * mm});
            skLineSegment(sketch, "E370", {"start": v(140.99, -74.72) * mm, "end": v(141.14, -74.74) * mm});
            skLineSegment(sketch, "E371", {"start": v(141.14, -74.74) * mm, "end": v(141.14, -75.9) * mm});
            skLineSegment(sketch, "E372", {"start": v(141.14, -75.9) * mm, "end": v(130.07, -75.9) * mm});
            skLineSegment(sketch, "E373", {"start": v(130.07, -75.9) * mm, "end": v(130.02, -75.71) * mm});
            skLineSegment(sketch, "E374", {"start": v(130.02, -75.71) * mm, "end": v(129.64, -74.08) * mm});
            skLineSegment(sketch, "E375", {"start": v(129.64, -74.08) * mm, "end": v(129.62, -73.94) * mm});
            skLineSegment(sketch, "E376", {"start": v(129.62, -73.94) * mm, "end": v(129.59, -73.8) * mm});
            skLineSegment(sketch, "E377", {"start": v(129.59, -73.8) * mm, "end": v(129.47, -72.92) * mm});
            skLineSegment(sketch, "E378", {"start": v(129.47, -72.92) * mm, "end": v(129.47, -72.64) * mm});
            skLineSegment(sketch, "E379", {"start": v(129.47, -72.64) * mm, "end": v(129.47, -69.52) * mm});
            skLineSegment(sketch, "E380", {"start": v(129.47, -69.52) * mm, "end": v(129.47, -69) * mm});
            skLineSegment(sketch, "E381", {"start": v(129.47, -69) * mm, "end": v(129.2, -67.46) * mm});
            skLineSegment(sketch, "E382", {"start": v(129.2, -67.46) * mm, "end": v(128.6, -66.28) * mm});
            skLineSegment(sketch, "E383", {"start": v(128.6, -66.28) * mm, "end": v(128.42, -66.12) * mm});
            skLineSegment(sketch, "E384", {"start": v(128.42, -66.12) * mm, "end": v(128.25, -65.95) * mm});
            skLineSegment(sketch, "E385", {"start": v(128.25, -65.95) * mm, "end": v(127, -65.38) * mm});
            skLineSegment(sketch, "E386", {"start": v(127, -65.38) * mm, "end": v(125.34, -65.13) * mm});
            skLineSegment(sketch, "E387", {"start": v(125.34, -65.13) * mm, "end": v(124.8, -65.13) * mm});
            skLineSegment(sketch, "E388", {"start": v(124.8, -65.13) * mm, "end": v(120.13, -65.13) * mm});
            skLineSegment(sketch, "E389", {"start": v(120.13, -65.13) * mm, "end": v(120.13, -75.9) * mm});
            skLineSegment(sketch, "E390", {"start": v(120.13, -75.9) * mm, "end": v(109.3, -75.9) * mm});
            skSolve(sketch);
        }
        {
            var Q0;
            Q0=makeQuery(id+"F0.imprint","IMPRINT",FACE,{"disambiguationData":[TD([[makeQuery(id+"F0.imprint","IMPRINT",EDGE,{"derivedFrom":sQuery(id+"F0.wireOp",EDGE,"E72")}),-1.0]])]});
            var Q1;
            Q1=makeQuery(id+"F0.imprint","IMPRINT",FACE,{"disambiguationData":[TD([[makeQuery(id+"F0.imprint","IMPRINT",EDGE,{"derivedFrom":sQuery(id+"F0.wireOp",EDGE,"E0")}),-1.0]])]});
            var Q2;
            {var subQ0=sQuery(id+"F0.wireOp",EDGE,"E65");Q2=makeQuery(id+"F0.imprint","IMPRINT",FACE,{"disambiguationData":[TD([[makeQuery(id+"F0.imprint","IMPRINT",EDGE,{"derivedFrom":subQ0}),-1.0]])]});}
            var Q3;
            {var subQ0=sQuery(id+"F0.wireOp",EDGE,"E105");Q3=makeQuery(id+"F0.imprint","IMPRINT",FACE,{"disambiguationData":[TD([[makeQuery(id+"F0.imprint","IMPRINT",EDGE,{"derivedFrom":subQ0}),-1.0]])]});}
            var Q4;
            {var subQ0=sQuery(id+"F0.wireOp",EDGE,"E145");Q4=makeQuery(id+"F0.imprint","IMPRINT",FACE,{"disambiguationData":[TD([[makeQuery(id+"F0.imprint","IMPRINT",EDGE,{"derivedFrom":subQ0}),-1.0]])]});}
            var Q5;
            {var subQ5=sQuery(id+"F0.wireOp",EDGE,"E165");Q5=makeQuery(id+"F0.imprint","IMPRINT",FACE,{"disambiguationData":[TD([[makeQuery(id+"F0.imprint","IMPRINT",EDGE,{"derivedFrom":subQ5}),-1.0]])]});}
            var Q6;
            Q6=makeQuery(id+"F0.imprint","IMPRINT",FACE,{"disambiguationData":[TD([[makeQuery(id+"F0.imprint","IMPRINT",EDGE,{"derivedFrom":sQuery(id+"F0.wireOp",EDGE,"E112")}),-1.0]])]});
            extrude(context, id + "F1", {"entities" : qUnion([Q0, Q1, Q2, Q3, Q4, Q5, Q6]), "oppositeDirection" : true, "depth" : 4.76 * mm, "offsetDistance" : 25.4 * mm});
        }
        {
            var Q0;
            Q0=makeQuery(id+"F1.opExtrude","SWEPT_FACE",FACE,{"disambiguationData":[OSD([sQuery(id+"F0.wireOp",EDGE,"E106"),sQuery(id+"F0.wireOp",EDGE,"E107"),sQuery(id+"F0.wireOp",EDGE,"E108")])]});
            var sketch = newSketch(context, id + "F2", { "sketchPlane" : qUnion([Q0])});
            skLineSegment(sketch, "E391.bottom", {"start": v(-133.83, -4.88) * mm, "end": v(126.9, -4.88) * mm});
            skLineSegment(sketch, "E391.top", {"start": v(-133.83, 50.69) * mm, "end": v(126.9, 50.69) * mm});
            skLineSegment(sketch, "E391.left", {"start": v(-133.83, -4.88) * mm, "end": v(-133.83, 50.69) * mm});
            skLineSegment(sketch, "E391.right", {"start": v(126.9, -4.88) * mm, "end": v(126.9, 50.69) * mm});
            skSolve(sketch);
        }
        {
            var Q0;
            Q0 = qSketchRegion(id + "F2", true);
            extrude(context, id + "F3", {"entities" : qUnion([Q0]), "depth" : 4.76 * mm, "offsetDistance" : 25.4 * mm});
        }
        {
            var Q0;
            Q0=makeQuery(id+"F3.opExtrude","CAP_FACE",FACE,{"disambiguationData":[OSD([sQuery(id+"F2.wireOp",EDGE,"E391.bottom"),sQuery(id+"F2.wireOp",EDGE,"E391.top"),sQuery(id+"F2.wireOp",EDGE,"E391.left"),sQuery(id+"F2.wireOp",EDGE,"E391.right")])],"isStart":false});
            var sketch = newSketch(context, id + "F4", { "sketchPlane" : qUnion([Q0])});
            skLineSegment(sketch, "E392.bottom", {"start": v(-133.83, 50.69) * mm, "end": v(126.9, 50.69) * mm});
            skLineSegment(sketch, "E392.top", {"start": v(-133.83, 45.92) * mm, "end": v(126.9, 45.92) * mm});
            skLineSegment(sketch, "E392.left", {"start": v(-133.83, 50.69) * mm, "end": v(-133.83, 45.92) * mm});
            skLineSegment(sketch, "E392.right", {"start": v(126.9, 50.69) * mm, "end": v(126.9, 45.92) * mm});
            skSolve(sketch);
        }
        {
            var Q0;
            Q0=makeQuery(id+"FS8kLoiKC918kTS_4.boolean.opBoolean","MERGE",FACE,{"derivedFrom":[makeQuery(id+"F3.opExtrude","SWEPT_FACE",FACE,{"disambiguationData":[OSD([sQuery(id+"F2.wireOp",EDGE,"E391.top")])]}),makeQuery(id+"FS8kLoiKC918kTS_4.opExtrude","SWEPT_FACE",FACE,{"disambiguationData":[OSD([sQuery(id+"F4.wireOp",EDGE,"E392.bottom")])]})]});
            var sketch = newSketch(context, id + "F5", { "sketchPlane" : qUnion([Q0])});
            skLineSegment(sketch, "E393", {"start": v(-123.16, -51.15) * mm, "end": v(-123.16, -6.7) * mm});
            skLineSegment(sketch, "E394", {"start": v(-123.16, -6.7) * mm, "end": v(-86.32, -6.7) * mm});
            skLineSegment(sketch, "E395", {"start": v(-86.32, -6.7) * mm, "end": v(-86.32, -17.9) * mm});
            skLineSegment(sketch, "E396", {"start": v(-86.32, -17.9) * mm, "end": v(-107.52, -17.9) * mm});
            skLineSegment(sketch, "E397", {"start": v(-107.52, -17.9) * mm, "end": v(-107.52, -24.78) * mm});
            skLineSegment(sketch, "E398", {"start": v(-107.52, -24.78) * mm, "end": v(-90.66, -24.78) * mm});
            skLineSegment(sketch, "E399", {"start": v(-90.66, -24.78) * mm, "end": v(-90.66, -35.52) * mm});
            skLineSegment(sketch, "E400", {"start": v(-90.66, -35.52) * mm, "end": v(-107.52, -35.52) * mm});
            skLineSegment(sketch, "E401", {"start": v(-107.52, -35.52) * mm, "end": v(-107.52, -51.15) * mm});
            skLineSegment(sketch, "E402", {"start": v(-107.52, -51.15) * mm, "end": v(-123.16, -51.15) * mm});
            skLineSegment(sketch, "E403", {"start": v(-80.37, -51.15) * mm, "end": v(-80.37, -6.7) * mm});
            skLineSegment(sketch, "E404", {"start": v(-80.37, -6.7) * mm, "end": v(-64.72, -6.7) * mm});
            skLineSegment(sketch, "E405", {"start": v(-64.72, -6.7) * mm, "end": v(-64.72, -39.35) * mm});
            skLineSegment(sketch, "E406", {"start": v(-64.72, -39.35) * mm, "end": v(-43.45, -39.35) * mm});
            skLineSegment(sketch, "E407", {"start": v(-43.45, -39.35) * mm, "end": v(-43.45, -51.15) * mm});
            skLineSegment(sketch, "E408", {"start": v(-43.45, -51.15) * mm, "end": v(-80.37, -51.15) * mm});
            skLineSegment(sketch, "E409", {"start": v(-25.8, -28.96) * mm, "end": v(-25.8, -30.33) * mm});
            skLineSegment(sketch, "E410", {"start": v(-25.8, -30.33) * mm, "end": v(-25.23, -34.43) * mm});
            skLineSegment(sketch, "E411", {"start": v(-25.23, -34.43) * mm, "end": v(-23.88, -37.74) * mm});
            skLineSegment(sketch, "E412", {"start": v(-23.88, -37.74) * mm, "end": v(-23.5, -38.24) * mm});
            skLineSegment(sketch, "E413", {"start": v(-23.5, -38.24) * mm, "end": v(-23.1, -38.73) * mm});
            skLineSegment(sketch, "E414", {"start": v(-23.1, -38.73) * mm, "end": v(-20.52, -40.45) * mm});
            skLineSegment(sketch, "E415", {"start": v(-20.52, -40.45) * mm, "end": v(-17.31, -41.19) * mm});
            skLineSegment(sketch, "E416", {"start": v(-17.31, -41.19) * mm, "end": v(-16.24, -41.19) * mm});
            skLineSegment(sketch, "E417", {"start": v(-16.24, -41.19) * mm, "end": v(-15.18, -41.19) * mm});
            skLineSegment(sketch, "E418", {"start": v(-15.18, -41.19) * mm, "end": v(-12, -40.46) * mm});
            skLineSegment(sketch, "E419", {"start": v(-12, -40.46) * mm, "end": v(-9.45, -38.74) * mm});
            skLineSegment(sketch, "E420", {"start": v(-9.45, -38.74) * mm, "end": v(-9.07, -38.25) * mm});
            skLineSegment(sketch, "E421", {"start": v(-9.07, -38.25) * mm, "end": v(-8.69, -37.75) * mm});
            skLineSegment(sketch, "E422", {"start": v(-8.69, -37.75) * mm, "end": v(-7.36, -34.46) * mm});
            skLineSegment(sketch, "E423", {"start": v(-7.36, -34.46) * mm, "end": v(-6.79, -30.33) * mm});
            skLineSegment(sketch, "E424", {"start": v(-6.79, -30.33) * mm, "end": v(-6.79, -28.96) * mm});
            skLineSegment(sketch, "E425", {"start": v(-6.79, -28.96) * mm, "end": v(-6.79, -27.58) * mm});
            skLineSegment(sketch, "E426", {"start": v(-6.79, -27.58) * mm, "end": v(-7.36, -23.45) * mm});
            skLineSegment(sketch, "E427", {"start": v(-7.36, -23.45) * mm, "end": v(-8.69, -20.15) * mm});
            skLineSegment(sketch, "E428", {"start": v(-8.69, -20.15) * mm, "end": v(-9.07, -19.66) * mm});
            skLineSegment(sketch, "E429", {"start": v(-9.07, -19.66) * mm, "end": v(-9.45, -19.16) * mm});
            skLineSegment(sketch, "E430", {"start": v(-9.45, -19.16) * mm, "end": v(-12, -17.44) * mm});
            skLineSegment(sketch, "E431", {"start": v(-12, -17.44) * mm, "end": v(-15.18, -16.71) * mm});
            skLineSegment(sketch, "E432", {"start": v(-15.18, -16.71) * mm, "end": v(-16.24, -16.71) * mm});
            skLineSegment(sketch, "E433", {"start": v(-16.24, -16.71) * mm, "end": v(-17.31, -16.71) * mm});
            skLineSegment(sketch, "E434", {"start": v(-17.31, -16.71) * mm, "end": v(-20.52, -17.45) * mm});
            skLineSegment(sketch, "E435", {"start": v(-20.52, -17.45) * mm, "end": v(-23.1, -19.18) * mm});
            skLineSegment(sketch, "E436", {"start": v(-23.1, -19.18) * mm, "end": v(-23.5, -19.67) * mm});
            skLineSegment(sketch, "E437", {"start": v(-23.5, -19.67) * mm, "end": v(-23.88, -20.16) * mm});
            skLineSegment(sketch, "E438", {"start": v(-23.88, -20.16) * mm, "end": v(-25.23, -23.47) * mm});
            skLineSegment(sketch, "E439", {"start": v(-25.23, -23.47) * mm, "end": v(-25.8, -27.59) * mm});
            skLineSegment(sketch, "E440", {"start": v(-25.8, -27.59) * mm, "end": v(-25.8, -28.96) * mm});
            skLineSegment(sketch, "E441", {"start": v(-41.57, -28.96) * mm, "end": v(-41.57, -26.53) * mm});
            skLineSegment(sketch, "E442", {"start": v(-41.57, -26.53) * mm, "end": v(-39.87, -19.24) * mm});
            skLineSegment(sketch, "E443", {"start": v(-39.87, -19.24) * mm, "end": v(-35.91, -12.87) * mm});
            skLineSegment(sketch, "E444", {"start": v(-35.91, -12.87) * mm, "end": v(-34.78, -11.82) * mm});
            skLineSegment(sketch, "E445", {"start": v(-34.78, -11.82) * mm, "end": v(-33.65, -10.78) * mm});
            skLineSegment(sketch, "E446", {"start": v(-33.65, -10.78) * mm, "end": v(-26.75, -7.11) * mm});
            skLineSegment(sketch, "E447", {"start": v(-26.75, -7.11) * mm, "end": v(-18.87, -5.55) * mm});
            skLineSegment(sketch, "E448", {"start": v(-18.87, -5.55) * mm, "end": v(-16.24, -5.55) * mm});
            skLineSegment(sketch, "E449", {"start": v(-16.24, -5.55) * mm, "end": v(-13.63, -5.55) * mm});
            skLineSegment(sketch, "E450", {"start": v(-13.63, -5.55) * mm, "end": v(-5.77, -7.11) * mm});
            skLineSegment(sketch, "E451", {"start": v(-5.77, -7.11) * mm, "end": v(1.1, -10.78) * mm});
            skLineSegment(sketch, "E452", {"start": v(1.1, -10.78) * mm, "end": v(2.23, -11.82) * mm});
            skLineSegment(sketch, "E453", {"start": v(2.23, -11.82) * mm, "end": v(3.37, -12.87) * mm});
            skLineSegment(sketch, "E454", {"start": v(3.37, -12.87) * mm, "end": v(7.32, -19.24) * mm});
            skLineSegment(sketch, "E455", {"start": v(7.32, -19.24) * mm, "end": v(9.02, -26.53) * mm});
            skLineSegment(sketch, "E456", {"start": v(9.02, -26.53) * mm, "end": v(9.02, -28.96) * mm});
            skLineSegment(sketch, "E457", {"start": v(9.02, -28.96) * mm, "end": v(9.02, -31.39) * mm});
            skLineSegment(sketch, "E458", {"start": v(9.02, -31.39) * mm, "end": v(7.32, -38.67) * mm});
            skLineSegment(sketch, "E459", {"start": v(7.32, -38.67) * mm, "end": v(3.37, -45.05) * mm});
            skLineSegment(sketch, "E460", {"start": v(3.37, -45.05) * mm, "end": v(2.23, -46.1) * mm});
            skLineSegment(sketch, "E461", {"start": v(2.23, -46.1) * mm, "end": v(1.1, -47.14) * mm});
            skLineSegment(sketch, "E462", {"start": v(1.1, -47.14) * mm, "end": v(-5.77, -50.81) * mm});
            skLineSegment(sketch, "E463", {"start": v(-5.77, -50.81) * mm, "end": v(-13.63, -52.39) * mm});
            skLineSegment(sketch, "E464", {"start": v(-13.63, -52.39) * mm, "end": v(-16.24, -52.39) * mm});
            skLineSegment(sketch, "E465", {"start": v(-16.24, -52.39) * mm, "end": v(-18.87, -52.39) * mm});
            skLineSegment(sketch, "E466", {"start": v(-18.87, -52.39) * mm, "end": v(-26.75, -50.81) * mm});
            skLineSegment(sketch, "E467", {"start": v(-26.75, -50.81) * mm, "end": v(-33.65, -47.14) * mm});
            skLineSegment(sketch, "E468", {"start": v(-33.65, -47.14) * mm, "end": v(-34.78, -46.1) * mm});
            skLineSegment(sketch, "E469", {"start": v(-34.78, -46.1) * mm, "end": v(-35.91, -45.05) * mm});
            skLineSegment(sketch, "E470", {"start": v(-35.91, -45.05) * mm, "end": v(-39.87, -38.67) * mm});
            skLineSegment(sketch, "E471", {"start": v(-39.87, -38.67) * mm, "end": v(-41.57, -31.39) * mm});
            skLineSegment(sketch, "E472", {"start": v(-41.57, -31.39) * mm, "end": v(-41.57, -28.96) * mm});
            skLineSegment(sketch, "E473", {"start": v(29.86, -28.96) * mm, "end": v(29.86, -30.33) * mm});
            skLineSegment(sketch, "E474", {"start": v(29.86, -30.33) * mm, "end": v(30.43, -34.43) * mm});
            skLineSegment(sketch, "E475", {"start": v(30.43, -34.43) * mm, "end": v(31.78, -37.74) * mm});
            skLineSegment(sketch, "E476", {"start": v(31.78, -37.74) * mm, "end": v(32.17, -38.24) * mm});
            skLineSegment(sketch, "E477", {"start": v(32.17, -38.24) * mm, "end": v(32.55, -38.73) * mm});
            skLineSegment(sketch, "E478", {"start": v(32.55, -38.73) * mm, "end": v(35.14, -40.45) * mm});
            skLineSegment(sketch, "E479", {"start": v(35.14, -40.45) * mm, "end": v(38.35, -41.19) * mm});
            skLineSegment(sketch, "E480", {"start": v(38.35, -41.19) * mm, "end": v(39.42, -41.19) * mm});
            skLineSegment(sketch, "E481", {"start": v(39.42, -41.19) * mm, "end": v(40.47, -41.19) * mm});
            skLineSegment(sketch, "E482", {"start": v(40.47, -41.19) * mm, "end": v(43.66, -40.46) * mm});
            skLineSegment(sketch, "E483", {"start": v(43.66, -40.46) * mm, "end": v(46.21, -38.74) * mm});
            skLineSegment(sketch, "E484", {"start": v(46.21, -38.74) * mm, "end": v(46.6, -38.25) * mm});
            skLineSegment(sketch, "E485", {"start": v(46.6, -38.25) * mm, "end": v(46.98, -37.75) * mm});
            skLineSegment(sketch, "E486", {"start": v(46.98, -37.75) * mm, "end": v(48.3, -34.46) * mm});
            skLineSegment(sketch, "E487", {"start": v(48.3, -34.46) * mm, "end": v(48.88, -30.33) * mm});
            skLineSegment(sketch, "E488", {"start": v(48.88, -30.33) * mm, "end": v(48.88, -28.96) * mm});
            skLineSegment(sketch, "E489", {"start": v(48.88, -28.96) * mm, "end": v(48.88, -27.58) * mm});
            skLineSegment(sketch, "E490", {"start": v(48.88, -27.58) * mm, "end": v(48.3, -23.45) * mm});
            skLineSegment(sketch, "E491", {"start": v(48.3, -23.45) * mm, "end": v(46.98, -20.15) * mm});
            skLineSegment(sketch, "E492", {"start": v(46.98, -20.15) * mm, "end": v(46.6, -19.66) * mm});
            skLineSegment(sketch, "E493", {"start": v(46.6, -19.66) * mm, "end": v(46.21, -19.16) * mm});
            skLineSegment(sketch, "E494", {"start": v(46.21, -19.16) * mm, "end": v(43.66, -17.44) * mm});
            skLineSegment(sketch, "E495", {"start": v(43.66, -17.44) * mm, "end": v(40.47, -16.71) * mm});
            skLineSegment(sketch, "E496", {"start": v(40.47, -16.71) * mm, "end": v(39.42, -16.71) * mm});
            skLineSegment(sketch, "E497", {"start": v(39.42, -16.71) * mm, "end": v(38.35, -16.71) * mm});
            skLineSegment(sketch, "E498", {"start": v(38.35, -16.71) * mm, "end": v(35.14, -17.45) * mm});
            skLineSegment(sketch, "E499", {"start": v(35.14, -17.45) * mm, "end": v(32.55, -19.18) * mm});
            skLineSegment(sketch, "E500", {"start": v(32.55, -19.18) * mm, "end": v(32.17, -19.67) * mm});
            skLineSegment(sketch, "E501", {"start": v(32.17, -19.67) * mm, "end": v(31.78, -20.16) * mm});
            skLineSegment(sketch, "E502", {"start": v(31.78, -20.16) * mm, "end": v(30.43, -23.47) * mm});
            skLineSegment(sketch, "E503", {"start": v(30.43, -23.47) * mm, "end": v(29.86, -27.59) * mm});
            skLineSegment(sketch, "E504", {"start": v(29.86, -27.59) * mm, "end": v(29.86, -28.96) * mm});
            skLineSegment(sketch, "E505", {"start": v(14.09, -28.96) * mm, "end": v(14.09, -26.53) * mm});
            skLineSegment(sketch, "E506", {"start": v(14.09, -26.53) * mm, "end": v(15.79, -19.24) * mm});
            skLineSegment(sketch, "E507", {"start": v(15.79, -19.24) * mm, "end": v(19.75, -12.87) * mm});
            skLineSegment(sketch, "E508", {"start": v(19.75, -12.87) * mm, "end": v(20.88, -11.82) * mm});
            skLineSegment(sketch, "E509", {"start": v(20.88, -11.82) * mm, "end": v(22.01, -10.78) * mm});
            skLineSegment(sketch, "E510", {"start": v(22.01, -10.78) * mm, "end": v(28.91, -7.11) * mm});
            skLineSegment(sketch, "E511", {"start": v(28.91, -7.11) * mm, "end": v(36.79, -5.55) * mm});
            skLineSegment(sketch, "E512", {"start": v(36.79, -5.55) * mm, "end": v(39.42, -5.55) * mm});
            skLineSegment(sketch, "E513", {"start": v(39.42, -5.55) * mm, "end": v(42.03, -5.55) * mm});
            skLineSegment(sketch, "E514", {"start": v(42.03, -5.55) * mm, "end": v(49.9, -7.11) * mm});
            skLineSegment(sketch, "E515", {"start": v(49.9, -7.11) * mm, "end": v(56.77, -10.78) * mm});
            skLineSegment(sketch, "E516", {"start": v(56.77, -10.78) * mm, "end": v(57.9, -11.82) * mm});
            skLineSegment(sketch, "E517", {"start": v(57.9, -11.82) * mm, "end": v(59.02, -12.87) * mm});
            skLineSegment(sketch, "E518", {"start": v(59.02, -12.87) * mm, "end": v(62.98, -19.24) * mm});
            skLineSegment(sketch, "E519", {"start": v(62.98, -19.24) * mm, "end": v(64.68, -26.53) * mm});
            skLineSegment(sketch, "E520", {"start": v(64.68, -26.53) * mm, "end": v(64.68, -28.96) * mm});
            skLineSegment(sketch, "E521", {"start": v(64.68, -28.96) * mm, "end": v(64.68, -31.39) * mm});
            skLineSegment(sketch, "E522", {"start": v(64.68, -31.39) * mm, "end": v(62.98, -38.67) * mm});
            skLineSegment(sketch, "E523", {"start": v(62.98, -38.67) * mm, "end": v(59.02, -45.05) * mm});
            skLineSegment(sketch, "E524", {"start": v(59.02, -45.05) * mm, "end": v(57.9, -46.1) * mm});
            skLineSegment(sketch, "E525", {"start": v(57.9, -46.1) * mm, "end": v(56.77, -47.14) * mm});
            skLineSegment(sketch, "E526", {"start": v(56.77, -47.14) * mm, "end": v(49.9, -50.81) * mm});
            skLineSegment(sketch, "E527", {"start": v(49.9, -50.81) * mm, "end": v(42.03, -52.39) * mm});
            skLineSegment(sketch, "E528", {"start": v(42.03, -52.39) * mm, "end": v(39.42, -52.39) * mm});
            skLineSegment(sketch, "E529", {"start": v(39.42, -52.39) * mm, "end": v(36.79, -52.39) * mm});
            skLineSegment(sketch, "E530", {"start": v(36.79, -52.39) * mm, "end": v(28.91, -50.81) * mm});
            skLineSegment(sketch, "E531", {"start": v(28.91, -50.81) * mm, "end": v(22.01, -47.14) * mm});
            skLineSegment(sketch, "E532", {"start": v(22.01, -47.14) * mm, "end": v(20.88, -46.1) * mm});
            skLineSegment(sketch, "E533", {"start": v(20.88, -46.1) * mm, "end": v(19.75, -45.05) * mm});
            skLineSegment(sketch, "E534", {"start": v(19.75, -45.05) * mm, "end": v(15.79, -38.67) * mm});
            skLineSegment(sketch, "E535", {"start": v(15.79, -38.67) * mm, "end": v(14.09, -31.39) * mm});
            skLineSegment(sketch, "E536", {"start": v(14.09, -31.39) * mm, "end": v(14.09, -28.96) * mm});
            skLineSegment(sketch, "E537", {"start": v(87.27, -25.8) * mm, "end": v(94.38, -25.8) * mm});
            skLineSegment(sketch, "E538", {"start": v(94.38, -25.8) * mm, "end": v(95.17, -25.8) * mm});
            skLineSegment(sketch, "E539", {"start": v(95.17, -25.8) * mm, "end": v(97.54, -25.57) * mm});
            skLineSegment(sketch, "E540", {"start": v(97.54, -25.57) * mm, "end": v(99.3, -25.03) * mm});
            skLineSegment(sketch, "E541", {"start": v(99.3, -25.03) * mm, "end": v(99.54, -24.88) * mm});
            skLineSegment(sketch, "E542", {"start": v(99.54, -24.88) * mm, "end": v(99.78, -24.73) * mm});
            skLineSegment(sketch, "E543", {"start": v(99.78, -24.73) * mm, "end": v(100.6, -23.61) * mm});
            skLineSegment(sketch, "E544", {"start": v(100.6, -23.61) * mm, "end": v(100.96, -22.15) * mm});
            skLineSegment(sketch, "E545", {"start": v(100.96, -22.15) * mm, "end": v(100.96, -21.67) * mm});
            skLineSegment(sketch, "E546", {"start": v(100.96, -21.67) * mm, "end": v(100.96, -21.17) * mm});
            skLineSegment(sketch, "E547", {"start": v(100.96, -21.17) * mm, "end": v(100.6, -19.67) * mm});
            skLineSegment(sketch, "E548", {"start": v(100.6, -19.67) * mm, "end": v(99.78, -18.55) * mm});
            skLineSegment(sketch, "E549", {"start": v(99.78, -18.55) * mm, "end": v(99.54, -18.4) * mm});
            skLineSegment(sketch, "E550", {"start": v(99.54, -18.4) * mm, "end": v(99.3, -18.24) * mm});
            skLineSegment(sketch, "E551", {"start": v(99.3, -18.24) * mm, "end": v(97.44, -17.7) * mm});
            skLineSegment(sketch, "E552", {"start": v(97.44, -17.7) * mm, "end": v(94.85, -17.47) * mm});
            skLineSegment(sketch, "E553", {"start": v(94.85, -17.47) * mm, "end": v(93.98, -17.47) * mm});
            skLineSegment(sketch, "E554", {"start": v(93.98, -17.47) * mm, "end": v(87.27, -17.47) * mm});
            skLineSegment(sketch, "E555", {"start": v(87.27, -17.47) * mm, "end": v(87.27, -25.8) * mm});
            skLineSegment(sketch, "E556", {"start": v(71.83, -51.15) * mm, "end": v(71.83, -6.7) * mm});
            skLineSegment(sketch, "E557", {"start": v(71.83, -6.7) * mm, "end": v(95.14, -6.7) * mm});
            skLineSegment(sketch, "E558", {"start": v(95.14, -6.7) * mm, "end": v(97.48, -6.7) * mm});
            skLineSegment(sketch, "E559", {"start": v(97.48, -6.7) * mm, "end": v(104.52, -7.45) * mm});
            skLineSegment(sketch, "E560", {"start": v(104.52, -7.45) * mm, "end": v(109.98, -9.19) * mm});
            skLineSegment(sketch, "E561", {"start": v(109.98, -9.19) * mm, "end": v(110.77, -9.69) * mm});
            skLineSegment(sketch, "E562", {"start": v(110.77, -9.69) * mm, "end": v(111.32, -10.04) * mm});
            skLineSegment(sketch, "E563", {"start": v(111.32, -10.04) * mm, "end": v(112.81, -11.42) * mm});
            skLineSegment(sketch, "E564", {"start": v(112.81, -11.42) * mm, "end": v(114.27, -13.63) * mm});
            skLineSegment(sketch, "E565", {"start": v(114.27, -13.63) * mm, "end": v(115.15, -16.32) * mm});
            skLineSegment(sketch, "E566", {"start": v(115.15, -16.32) * mm, "end": v(115.44, -18.7) * mm});
            skLineSegment(sketch, "E567", {"start": v(115.44, -18.7) * mm, "end": v(115.44, -19.5) * mm});
            skLineSegment(sketch, "E568", {"start": v(115.44, -19.5) * mm, "end": v(115.44, -20.42) * mm});
            skLineSegment(sketch, "E569", {"start": v(115.44, -20.42) * mm, "end": v(114.96, -23.22) * mm});
            skLineSegment(sketch, "E570", {"start": v(114.96, -23.22) * mm, "end": v(113.84, -25.8) * mm});
            skLineSegment(sketch, "E571", {"start": v(113.84, -25.8) * mm, "end": v(113.52, -26.25) * mm});
            skLineSegment(sketch, "E572", {"start": v(113.52, -26.25) * mm, "end": v(113.2, -26.7) * mm});
            skLineSegment(sketch, "E573", {"start": v(113.2, -26.7) * mm, "end": v(111.09, -28.66) * mm});
            skLineSegment(sketch, "E574", {"start": v(111.09, -28.66) * mm, "end": v(108.27, -30.25) * mm});
            skLineSegment(sketch, "E575", {"start": v(108.27, -30.25) * mm, "end": v(107.6, -30.5) * mm});
            skLineSegment(sketch, "E576", {"start": v(107.6, -30.5) * mm, "end": v(108.29, -30.64) * mm});
            skLineSegment(sketch, "E577", {"start": v(108.29, -30.64) * mm, "end": v(111.12, -31.68) * mm});
            skLineSegment(sketch, "E578", {"start": v(111.12, -31.68) * mm, "end": v(113.21, -33.22) * mm});
            skLineSegment(sketch, "E579", {"start": v(113.21, -33.22) * mm, "end": v(113.52, -33.6) * mm});
            skLineSegment(sketch, "E580", {"start": v(113.52, -33.6) * mm, "end": v(113.83, -33.99) * mm});
            skLineSegment(sketch, "E581", {"start": v(113.83, -33.99) * mm, "end": v(114.95, -36.45) * mm});
            skLineSegment(sketch, "E582", {"start": v(114.95, -36.45) * mm, "end": v(115.48, -39.63) * mm});
            skLineSegment(sketch, "E583", {"start": v(115.48, -39.63) * mm, "end": v(115.5, -40.38) * mm});
            skLineSegment(sketch, "E584", {"start": v(115.5, -40.38) * mm, "end": v(115.77, -46.57) * mm});
            skLineSegment(sketch, "E585", {"start": v(115.77, -46.57) * mm, "end": v(115.77, -46.6) * mm});
            skLineSegment(sketch, "E586", {"start": v(115.77, -46.6) * mm, "end": v(115.8, -46.7) * mm});
            skLineSegment(sketch, "E587", {"start": v(115.8, -46.7) * mm, "end": v(115.8, -46.7) * mm});
            skLineSegment(sketch, "E588", {"start": v(115.8, -46.7) * mm, "end": v(115.82, -47.15) * mm});
            skLineSegment(sketch, "E589", {"start": v(115.82, -47.15) * mm, "end": v(116.2, -48.74) * mm});
            skLineSegment(sketch, "E590", {"start": v(116.2, -48.74) * mm, "end": v(116.98, -49.47) * mm});
            skLineSegment(sketch, "E591", {"start": v(116.98, -49.47) * mm, "end": v(117.2, -49.5) * mm});
            skLineSegment(sketch, "E592", {"start": v(117.2, -49.5) * mm, "end": v(117.2, -51.15) * mm});
            skLineSegment(sketch, "E593", {"start": v(117.2, -51.15) * mm, "end": v(101.42, -51.15) * mm});
            skLineSegment(sketch, "E594", {"start": v(101.42, -51.15) * mm, "end": v(101.35, -50.89) * mm});
            skLineSegment(sketch, "E595", {"start": v(101.35, -50.89) * mm, "end": v(100.82, -48.56) * mm});
            skLineSegment(sketch, "E596", {"start": v(100.82, -48.56) * mm, "end": v(100.78, -48.36) * mm});
            skLineSegment(sketch, "E597", {"start": v(100.78, -48.36) * mm, "end": v(100.74, -48.16) * mm});
            skLineSegment(sketch, "E598", {"start": v(100.74, -48.16) * mm, "end": v(100.57, -46.92) * mm});
            skLineSegment(sketch, "E599", {"start": v(100.57, -46.92) * mm, "end": v(100.57, -46.5) * mm});
            skLineSegment(sketch, "E600", {"start": v(100.57, -46.5) * mm, "end": v(100.57, -42.07) * mm});
            skLineSegment(sketch, "E601", {"start": v(100.57, -42.07) * mm, "end": v(100.57, -41.33) * mm});
            skLineSegment(sketch, "E602", {"start": v(100.57, -41.33) * mm, "end": v(100.2, -39.14) * mm});
            skLineSegment(sketch, "E603", {"start": v(100.2, -39.14) * mm, "end": v(99.32, -37.46) * mm});
            skLineSegment(sketch, "E604", {"start": v(99.32, -37.46) * mm, "end": v(99.08, -37.22) * mm});
            skLineSegment(sketch, "E605", {"start": v(99.08, -37.22) * mm, "end": v(98.83, -36.99) * mm});
            skLineSegment(sketch, "E606", {"start": v(98.83, -36.99) * mm, "end": v(97.04, -36.17) * mm});
            skLineSegment(sketch, "E607", {"start": v(97.04, -36.17) * mm, "end": v(94.7, -35.82) * mm});
            skLineSegment(sketch, "E608", {"start": v(94.7, -35.82) * mm, "end": v(93.91, -35.82) * mm});
            skLineSegment(sketch, "E609", {"start": v(93.91, -35.82) * mm, "end": v(87.27, -35.82) * mm});
            skLineSegment(sketch, "E610", {"start": v(87.27, -35.82) * mm, "end": v(87.27, -51.15) * mm});
            skLineSegment(sketch, "E611", {"start": v(87.27, -51.15) * mm, "end": v(71.83, -51.15) * mm});
            skSolve(sketch);
        }
        {
            var Q0;
            {var subQ0=sQuery(id+"F5.wireOp",EDGE,"E396");Q0=makeQuery(id+"F5.imprint","IMPRINT",FACE,{"disambiguationData":[TD([[makeQuery(id+"F5.imprint","IMPRINT",EDGE,{"derivedFrom":subQ0}),-1.0]])]});}
            var Q1;
            {var subQ0=sQuery(id+"F5.wireOp",EDGE,"E406");Q1=makeQuery(id+"F5.imprint","IMPRINT",FACE,{"disambiguationData":[TD([[makeQuery(id+"F5.imprint","IMPRINT",EDGE,{"derivedFrom":subQ0}),-1.0]])]});}
            var Q2;
            Q2=makeQuery(id+"F5.imprint","IMPRINT",FACE,{"disambiguationData":[TD([[makeQuery(id+"F5.imprint","IMPRINT",EDGE,{"derivedFrom":sQuery(id+"F5.wireOp",EDGE,"E409")}),-1.0]])]});
            var Q3;
            Q3=makeQuery(id+"F5.imprint","IMPRINT",FACE,{"disambiguationData":[TD([[makeQuery(id+"F5.imprint","IMPRINT",EDGE,{"derivedFrom":sQuery(id+"F5.wireOp",EDGE,"E473")}),-1.0]])]});
            var Q4;
            Q4=makeQuery(id+"F5.imprint","IMPRINT",FACE,{"disambiguationData":[TD([[makeQuery(id+"F5.imprint","IMPRINT",EDGE,{"derivedFrom":sQuery(id+"F5.wireOp",EDGE,"E537")}),-1.0]])]});
            var Q5;
            Q5=sQuery(id+"F5.wireOp",EDGE,"E405");
            var Q6;
            Q6=sQuery(id+"F5.wireOp",EDGE,"E404");
            var Q7;
            Q7=sQuery(id+"F5.wireOp",EDGE,"E403");
            var Q8;
            Q8=sQuery(id+"F5.wireOp",EDGE,"E611");
            var Q9;
            Q9=sQuery(id+"F5.wireOp",EDGE,"E554");
            var Q10;
            Q10=sQuery(id+"F5.wireOp",EDGE,"E471");
            var Q11;
            Q11=sQuery(id+"F5.wireOp",EDGE,"E455");
            var Q12;
            Q12=sQuery(id+"F5.wireOp",EDGE,"E439");
            var Q13;
            Q13=sQuery(id+"F5.wireOp",EDGE,"E423");
            var Q14;
            Q14=sQuery(id+"F5.wireOp",EDGE,"E535");
            var Q15;
            Q15=sQuery(id+"F5.wireOp",EDGE,"E519");
            var Q16;
            Q16=sQuery(id+"F5.wireOp",EDGE,"E487");
            var Q17;
            Q17=sQuery(id+"F5.wireOp",EDGE,"E503");
            var Q18;
            Q18=sQuery(id+"F5.wireOp",EDGE,"E406");
            var Q19;
            Q19=sQuery(id+"F5.wireOp",EDGE,"E407");
            var Q20;
            Q20=sQuery(id+"F5.wireOp",EDGE,"E408");
            var Q21;
            Q21=sQuery(id+"F5.wireOp",EDGE,"E393");
            var Q22;
            Q22=sQuery(id+"F5.wireOp",EDGE,"E394");
            var Q23;
            Q23=sQuery(id+"F5.wireOp",EDGE,"E395");
            var Q24;
            Q24=sQuery(id+"F5.wireOp",EDGE,"E396");
            var Q25;
            Q25=sQuery(id+"F5.wireOp",EDGE,"E397");
            var Q26;
            Q26=sQuery(id+"F5.wireOp",EDGE,"E398");
            var Q27;
            Q27=sQuery(id+"F5.wireOp",EDGE,"E399");
            var Q28;
            Q28=sQuery(id+"F5.wireOp",EDGE,"E400");
            var Q29;
            Q29=sQuery(id+"F5.wireOp",EDGE,"E401");
            var Q30;
            Q30=sQuery(id+"F5.wireOp",EDGE,"E402");
            var Q31;
            Q31=sQuery(id+"F5.wireOp",EDGE,"E555");
            var Q32;
            Q32=sQuery(id+"F5.wireOp",EDGE,"E474");
            var Q33;
            Q33=sQuery(id+"F5.wireOp",EDGE,"E490");
            var Q34;
            Q34=sQuery(id+"F5.wireOp",EDGE,"E458");
            var Q35;
            Q35=sQuery(id+"F5.wireOp",EDGE,"E410");
            var Q36;
            Q36=sQuery(id+"F5.wireOp",EDGE,"E523");
            var Q37;
            Q37=sQuery(id+"F5.wireOp",EDGE,"E507");
            var Q38;
            Q38=sQuery(id+"F5.wireOp",EDGE,"E459");
            var Q39;
            Q39=sQuery(id+"F5.wireOp",EDGE,"E443");
            var Q40;
            Q40=sQuery(id+"F5.wireOp",EDGE,"E537");
            var Q41;
            Q41=sQuery(id+"F5.wireOp",EDGE,"E557");
            var Q42;
            Q42=sQuery(id+"F5.wireOp",EDGE,"E584");
            var Q43;
            Q43=sQuery(id+"F5.wireOp",EDGE,"E600");
            var Q44;
            Q44=sQuery(id+"F5.wireOp",EDGE,"E462");
            var Q45;
            Q45=sQuery(id+"F5.wireOp",EDGE,"E446");
            var Q46;
            Q46=sQuery(id+"F5.wireOp",EDGE,"E526");
            var Q47;
            Q47=sQuery(id+"F5.wireOp",EDGE,"E510");
            var Q48;
            Q48=sQuery(id+"F5.wireOp",EDGE,"E470");
            var Q49;
            Q49=sQuery(id+"F5.wireOp",EDGE,"E454");
            var Q50;
            Q50=sQuery(id+"F5.wireOp",EDGE,"E438");
            var Q51;
            Q51=sQuery(id+"F5.wireOp",EDGE,"E534");
            var Q52;
            Q52=sQuery(id+"F5.wireOp",EDGE,"E463");
            var Q53;
            Q53=sQuery(id+"F5.wireOp",EDGE,"E447");
            var Q54;
            Q54=sQuery(id+"F5.wireOp",EDGE,"E527");
            var Q55;
            Q55=sQuery(id+"F5.wireOp",EDGE,"E511");
            var Q56;
            Q56=sQuery(id+"F5.wireOp",EDGE,"E559");
            var Q57;
            Q57=sQuery(id+"F5.wireOp",EDGE,"E518");
            var Q58;
            Q58=sQuery(id+"F5.wireOp",EDGE,"E560");
            var Q59;
            Q59=sQuery(id+"F5.wireOp",EDGE,"E609");
            var Q60;
            Q60=sQuery(id+"F5.wireOp",EDGE,"E593");
            var Q61;
            Q61=sQuery(id+"F5.wireOp",EDGE,"E556");
            var Q62;
            Q62=sQuery(id+"F5.wireOp",EDGE,"E450");
            var Q63;
            Q63=sQuery(id+"F5.wireOp",EDGE,"E442");
            var Q64;
            Q64=sQuery(id+"F5.wireOp",EDGE,"E514");
            var Q65;
            Q65=sQuery(id+"F5.wireOp",EDGE,"E466");
            var Q66;
            Q66=sQuery(id+"F5.wireOp",EDGE,"E426");
            var Q67;
            Q67=sQuery(id+"F5.wireOp",EDGE,"E610");
            var Q68;
            Q68=sQuery(id+"F5.wireOp",EDGE,"E530");
            var Q69;
            Q69=sQuery(id+"F5.wireOp",EDGE,"E522");
            var Q70;
            Q70=sQuery(id+"F5.wireOp",EDGE,"E506");
            var Q71;
            Q71=sQuery(id+"F5.wireOp",EDGE,"E451");
            var Q72;
            Q72=sQuery(id+"F5.wireOp",EDGE,"E515");
            var Q73;
            Q73=sQuery(id+"F5.wireOp",EDGE,"E467");
            var Q74;
            Q74=sQuery(id+"F5.wireOp",EDGE,"E531");
            var Q75;
            Q75=sQuery(id+"F5.wireOp",EDGE,"E602");
            var Q76;
            Q76=sQuery(id+"F5.wireOp",EDGE,"E595");
            var Q77;
            Q77=sQuery(id+"F5.wireOp",EDGE,"E452");
            var Q78;
            Q78=sQuery(id+"F5.wireOp",EDGE,"E420");
            var Q79;
            Q79=sQuery(id+"F5.wireOp",EDGE,"E516");
            var Q80;
            Q80=sQuery(id+"F5.wireOp",EDGE,"E500");
            var Q81;
            Q81=sQuery(id+"F5.wireOp",EDGE,"E468");
            var Q82;
            Q82=sQuery(id+"F5.wireOp",EDGE,"E580");
            var Q83;
            Q83=sQuery(id+"F5.wireOp",EDGE,"E564");
            var Q84;
            Q84=sQuery(id+"F5.wireOp",EDGE,"E532");
            var Q85;
            Q85=sQuery(id+"F5.wireOp",EDGE,"E424");
            var Q86;
            Q86=sQuery(id+"F5.wireOp",EDGE,"E453");
            var Q87;
            Q87=sQuery(id+"F5.wireOp",EDGE,"E421");
            var Q88;
            Q88=sQuery(id+"F5.wireOp",EDGE,"E517");
            var Q89;
            Q89=sQuery(id+"F5.wireOp",EDGE,"E501");
            var Q90;
            Q90=sQuery(id+"F5.wireOp",EDGE,"E469");
            var Q91;
            Q91=sQuery(id+"F5.wireOp",EDGE,"E581");
            var Q92;
            Q92=sQuery(id+"F5.wireOp",EDGE,"E565");
            var Q93;
            Q93=sQuery(id+"F5.wireOp",EDGE,"E533");
            var Q94;
            Q94=sQuery(id+"F5.wireOp",EDGE,"E599");
            var Q95;
            Q95=sQuery(id+"F5.wireOp",EDGE,"E583");
            var Q96;
            Q96=sQuery(id+"F5.wireOp",EDGE,"E536");
            var Q97;
            Q97=sQuery(id+"F5.wireOp",EDGE,"E567");
            var Q98;
            Q98=sQuery(id+"F5.wireOp",EDGE,"E413");
            var Q99;
            Q99=sQuery(id+"F5.wireOp",EDGE,"E477");
            var Q100;
            Q100=sQuery(id+"F5.wireOp",EDGE,"E570");
            var Q101;
            Q101=sQuery(id+"F5.wireOp",EDGE,"E409");
            var Q102;
            Q102=sQuery(id+"F5.wireOp",EDGE,"E473");
            var Q103;
            Q103=sQuery(id+"F5.wireOp",EDGE,"E539");
            var Q104;
            Q104=sQuery(id+"F5.wireOp",EDGE,"E491");
            var Q105;
            Q105=sQuery(id+"F5.wireOp",EDGE,"E603");
            var Q106;
            Q106=sQuery(id+"F5.wireOp",EDGE,"E571");
            var Q107;
            Q107=sQuery(id+"F5.wireOp",EDGE,"E411");
            var Q108;
            Q108=sQuery(id+"F5.wireOp",EDGE,"E475");
            var Q109;
            Q109=sQuery(id+"F5.wireOp",EDGE,"E427");
            var Q110;
            Q110=sQuery(id+"F5.wireOp",EDGE,"E457");
            var Q111;
            Q111=sQuery(id+"F5.wireOp",EDGE,"E441");
            var Q112;
            Q112=sQuery(id+"F5.wireOp",EDGE,"E412");
            var Q113;
            Q113=sQuery(id+"F5.wireOp",EDGE,"E476");
            var Q114;
            Q114=sQuery(id+"F5.wireOp",EDGE,"E460");
            var Q115;
            Q115=sQuery(id+"F5.wireOp",EDGE,"E444");
            var Q116;
            Q116=sQuery(id+"F5.wireOp",EDGE,"E425");
            var Q117;
            Q117=sQuery(id+"F5.wireOp",EDGE,"E428");
            var Q118;
            Q118=sQuery(id+"F5.wireOp",EDGE,"E524");
            var Q119;
            Q119=sQuery(id+"F5.wireOp",EDGE,"E508");
            var Q120;
            Q120=sQuery(id+"F5.wireOp",EDGE,"E492");
            var Q121;
            Q121=sQuery(id+"F5.wireOp",EDGE,"E521");
            var Q122;
            Q122=sQuery(id+"F5.wireOp",EDGE,"E461");
            var Q123;
            Q123=sQuery(id+"F5.wireOp",EDGE,"E520");
            var Q124;
            Q124=sQuery(id+"F5.wireOp",EDGE,"E445");
            var Q125;
            Q125=sQuery(id+"F5.wireOp",EDGE,"E429");
            var Q126;
            Q126=sQuery(id+"F5.wireOp",EDGE,"E525");
            var Q127;
            Q127=sQuery(id+"F5.wireOp",EDGE,"E509");
            var Q128;
            Q128=sQuery(id+"F5.wireOp",EDGE,"E493");
            var Q129;
            Q129=sQuery(id+"F5.wireOp",EDGE,"E573");
            var Q130;
            Q130=sQuery(id+"F5.wireOp",EDGE,"E505");
            var Q131;
            Q131=sQuery(id+"F5.wireOp",EDGE,"E489");
            var Q132;
            Q132=sQuery(id+"F5.wireOp",EDGE,"E601");
            var Q133;
            Q133=sQuery(id+"F5.wireOp",EDGE,"E569");
            var Q134;
            Q134=sQuery(id+"F5.wireOp",EDGE,"E568");
            var Q135;
            Q135=sQuery(id+"F5.wireOp",EDGE,"E414");
            var Q136;
            Q136=sQuery(id+"F5.wireOp",EDGE,"E478");
            var Q137;
            Q137=sQuery(id+"F5.wireOp",EDGE,"E430");
            var Q138;
            Q138=sQuery(id+"F5.wireOp",EDGE,"E494");
            var Q139;
            Q139=sQuery(id+"F5.wireOp",EDGE,"E574");
            var Q140;
            Q140=sQuery(id+"F5.wireOp",EDGE,"E558");
            var Q141;
            Q141=sQuery(id+"F5.wireOp",EDGE,"E553");
            var Q142;
            Q142=sQuery(id+"F5.wireOp",EDGE,"E422");
            var Q143;
            Q143=sQuery(id+"F5.wireOp",EDGE,"E472");
            var Q144;
            Q144=sQuery(id+"F5.wireOp",EDGE,"E415");
            var Q145;
            Q145=sQuery(id+"F5.wireOp",EDGE,"E479");
            var Q146;
            Q146=sQuery(id+"F5.wireOp",EDGE,"E431");
            var Q147;
            Q147=sQuery(id+"F5.wireOp",EDGE,"E495");
            var Q148;
            Q148=sQuery(id+"F5.wireOp",EDGE,"E607");
            var Q149;
            Q149=sQuery(id+"F5.wireOp",EDGE,"E502");
            var Q150;
            Q150=sQuery(id+"F5.wireOp",EDGE,"E486");
            var Q151;
            Q151=sQuery(id+"F5.wireOp",EDGE,"E582");
            var Q152;
            Q152=sQuery(id+"F5.wireOp",EDGE,"E448");
            var Q153;
            Q153=sQuery(id+"F5.wireOp",EDGE,"E566");
            var Q154;
            Q154=sQuery(id+"F5.wireOp",EDGE,"E432");
            var Q155;
            Q155=sQuery(id+"F5.wireOp",EDGE,"E552");
            var Q156;
            Q156=sQuery(id+"F5.wireOp",EDGE,"E456");
            var Q157;
            Q157=sQuery(id+"F5.wireOp",EDGE,"E416");
            var Q158;
            Q158=sQuery(id+"F5.wireOp",EDGE,"E512");
            var Q159;
            Q159=sQuery(id+"F5.wireOp",EDGE,"E480");
            var Q160;
            Q160=sQuery(id+"F5.wireOp",EDGE,"E496");
            var Q161;
            Q161=sQuery(id+"F5.wireOp",EDGE,"E464");
            var Q162;
            Q162=sQuery(id+"F5.wireOp",EDGE,"E544");
            var Q163;
            Q163=sQuery(id+"F5.wireOp",EDGE,"E528");
            var Q164;
            Q164=sQuery(id+"F5.wireOp",EDGE,"E608");
            var Q165;
            Q165=sQuery(id+"F5.wireOp",EDGE,"E592");
            var Q166;
            Q166=sQuery(id+"F5.wireOp",EDGE,"E572");
            var Q167;
            Q167=sQuery(id+"F5.wireOp",EDGE,"E433");
            var Q168;
            Q168=sQuery(id+"F5.wireOp",EDGE,"E449");
            var Q169;
            Q169=sQuery(id+"F5.wireOp",EDGE,"E417");
            var Q170;
            Q170=sQuery(id+"F5.wireOp",EDGE,"E513");
            var Q171;
            Q171=sQuery(id+"F5.wireOp",EDGE,"E497");
            var Q172;
            Q172=sQuery(id+"F5.wireOp",EDGE,"E465");
            var Q173;
            Q173=sQuery(id+"F5.wireOp",EDGE,"E481");
            var Q174;
            Q174=sQuery(id+"F5.wireOp",EDGE,"E577");
            var Q175;
            Q175=sQuery(id+"F5.wireOp",EDGE,"E561");
            var Q176;
            Q176=sQuery(id+"F5.wireOp",EDGE,"E545");
            var Q177;
            Q177=sQuery(id+"F5.wireOp",EDGE,"E529");
            var Q178;
            Q178=sQuery(id+"F5.wireOp",EDGE,"E488");
            var Q179;
            Q179=sQuery(id+"F5.wireOp",EDGE,"E504");
            var Q180;
            Q180=sQuery(id+"F5.wireOp",EDGE,"E434");
            var Q181;
            Q181=sQuery(id+"F5.wireOp",EDGE,"E418");
            var Q182;
            Q182=sQuery(id+"F5.wireOp",EDGE,"E498");
            var Q183;
            Q183=sQuery(id+"F5.wireOp",EDGE,"E482");
            var Q184;
            Q184=sQuery(id+"F5.wireOp",EDGE,"E562");
            var Q185;
            Q185=sQuery(id+"F5.wireOp",EDGE,"E578");
            var Q186;
            Q186=sQuery(id+"F5.wireOp",EDGE,"E546");
            var Q187;
            Q187=sQuery(id+"F5.wireOp",EDGE,"E594");
            var Q188;
            Q188=sQuery(id+"F5.wireOp",EDGE,"E538");
            var Q189;
            Q189=sQuery(id+"F5.wireOp",EDGE,"E440");
            var Q190;
            Q190=sQuery(id+"F5.wireOp",EDGE,"E435");
            var Q191;
            Q191=sQuery(id+"F5.wireOp",EDGE,"E419");
            var Q192;
            Q192=sQuery(id+"F5.wireOp",EDGE,"E483");
            var Q193;
            Q193=sQuery(id+"F5.wireOp",EDGE,"E499");
            var Q194;
            Q194=sQuery(id+"F5.wireOp",EDGE,"E579");
            var Q195;
            Q195=sQuery(id+"F5.wireOp",EDGE,"E563");
            var Q196;
            Q196=sQuery(id+"F5.wireOp",EDGE,"E547");
            var Q197;
            Q197=sQuery(id+"F5.wireOp",EDGE,"E598");
            var Q198;
            Q198=sQuery(id+"F5.wireOp",EDGE,"E436");
            var Q199;
            Q199=sQuery(id+"F5.wireOp",EDGE,"E484");
            var Q200;
            Q200=sQuery(id+"F5.wireOp",EDGE,"E548");
            var Q201;
            Q201=sQuery(id+"F5.wireOp",EDGE,"E596");
            var Q202;
            Q202=sQuery(id+"F5.wireOp",EDGE,"E437");
            var Q203;
            Q203=sQuery(id+"F5.wireOp",EDGE,"E485");
            var Q204;
            Q204=sQuery(id+"F5.wireOp",EDGE,"E549");
            var Q205;
            Q205=sQuery(id+"F5.wireOp",EDGE,"E597");
            var Q206;
            Q206=sQuery(id+"F5.wireOp",EDGE,"E551");
            var Q207;
            Q207=sQuery(id+"F5.wireOp",EDGE,"E589");
            var Q208;
            Q208=sQuery(id+"F5.wireOp",EDGE,"E606");
            var Q209;
            Q209=sQuery(id+"F5.wireOp",EDGE,"E590");
            var Q210;
            Q210=sQuery(id+"F5.wireOp",EDGE,"E591");
            var Q211;
            Q211=sQuery(id+"F5.wireOp",EDGE,"E575");
            var Q212;
            Q212=sQuery(id+"F5.wireOp",EDGE,"E550");
            var Q213;
            Q213=sQuery(id+"F5.wireOp",EDGE,"E576");
            var Q214;
            Q214=sQuery(id+"F5.wireOp",EDGE,"E604");
            var Q215;
            Q215=sQuery(id+"F5.wireOp",EDGE,"E605");
            var Q216;
            Q216=sQuery(id+"F5.wireOp",EDGE,"E540");
            var Q217;
            Q217=sQuery(id+"F5.wireOp",EDGE,"E542");
            var Q218;
            Q218=sQuery(id+"F5.wireOp",EDGE,"E543");
            var Q219;
            Q219=sQuery(id+"F5.wireOp",EDGE,"E541");
            var Q220;
            Q220=sQuery(id+"F5.wireOp",EDGE,"E588");
            var Q221;
            Q221=sQuery(id+"F5.wireOp",EDGE,"E587");
            var Q222;
            Q222=sQuery(id+"F5.wireOp",EDGE,"E586");
            var Q223;
            Q223=sQuery(id+"F5.wireOp",EDGE,"E585");
            extrude(context, id + "F6", {"entities" : qUnion([Q0, Q1, Q2, Q3, Q4]), "surfaceEntities" : qUnion([Q5, Q6, Q7, Q8, Q9, Q10, Q11, Q12, Q13, Q14, Q15, Q16, Q17, Q18, Q19, Q20, Q21, Q22, Q23, Q24, Q25, Q26, Q27, Q28, Q29, Q30, Q31, Q32, Q33, Q34, Q35, Q36, Q37, Q38, Q39, Q40, Q41, Q42, Q43, Q44, Q45, Q46, Q47, Q48, Q49, Q50, Q51, Q52, Q53, Q54, Q55, Q56, Q57, Q58, Q59, Q60, Q61, Q62, Q63, Q64, Q65, Q66, Q67, Q68, Q69, Q70, Q71, Q72, Q73, Q74, Q75, Q76, Q77, Q78, Q79, Q80, Q81, Q82, Q83, Q84, Q85, Q86, Q87, Q88, Q89, Q90, Q91, Q92, Q93, Q94, Q95, Q96, Q97, Q98, Q99, Q100, Q101, Q102, Q103, Q104, Q105, Q106, Q107, Q108, Q109, Q110, Q111, Q112, Q113, Q114, Q115, Q116, Q117, Q118, Q119, Q120, Q121, Q122, Q123, Q124, Q125, Q126, Q127, Q128, Q129, Q130, Q131, Q132, Q133, Q134, Q135, Q136, Q137, Q138, Q139, Q140, Q141, Q142, Q143, Q144, Q145, Q146, Q147, Q148, Q149, Q150, Q151, Q152, Q153, Q154, Q155, Q156, Q157, Q158, Q159, Q160, Q161, Q162, Q163, Q164, Q165, Q166, Q167, Q168, Q169, Q170, Q171, Q172, Q173, Q174, Q175, Q176, Q177, Q178, Q179, Q180, Q181, Q182, Q183, Q184, Q185, Q186, Q187, Q188, Q189, Q190, Q191, Q192, Q193, Q194, Q195, Q196, Q197, Q198, Q199, Q200, Q201, Q202, Q203, Q204, Q205, Q206, Q207, Q208, Q209, Q210, Q211, Q212, Q213, Q214, Q215, Q216, Q217, Q218, Q219, Q220, Q221, Q222, Q223]), "oppositeDirection" : true, "depth" : 4.76 * mm, "offsetDistance" : 25.4 * mm});
        }
    });
